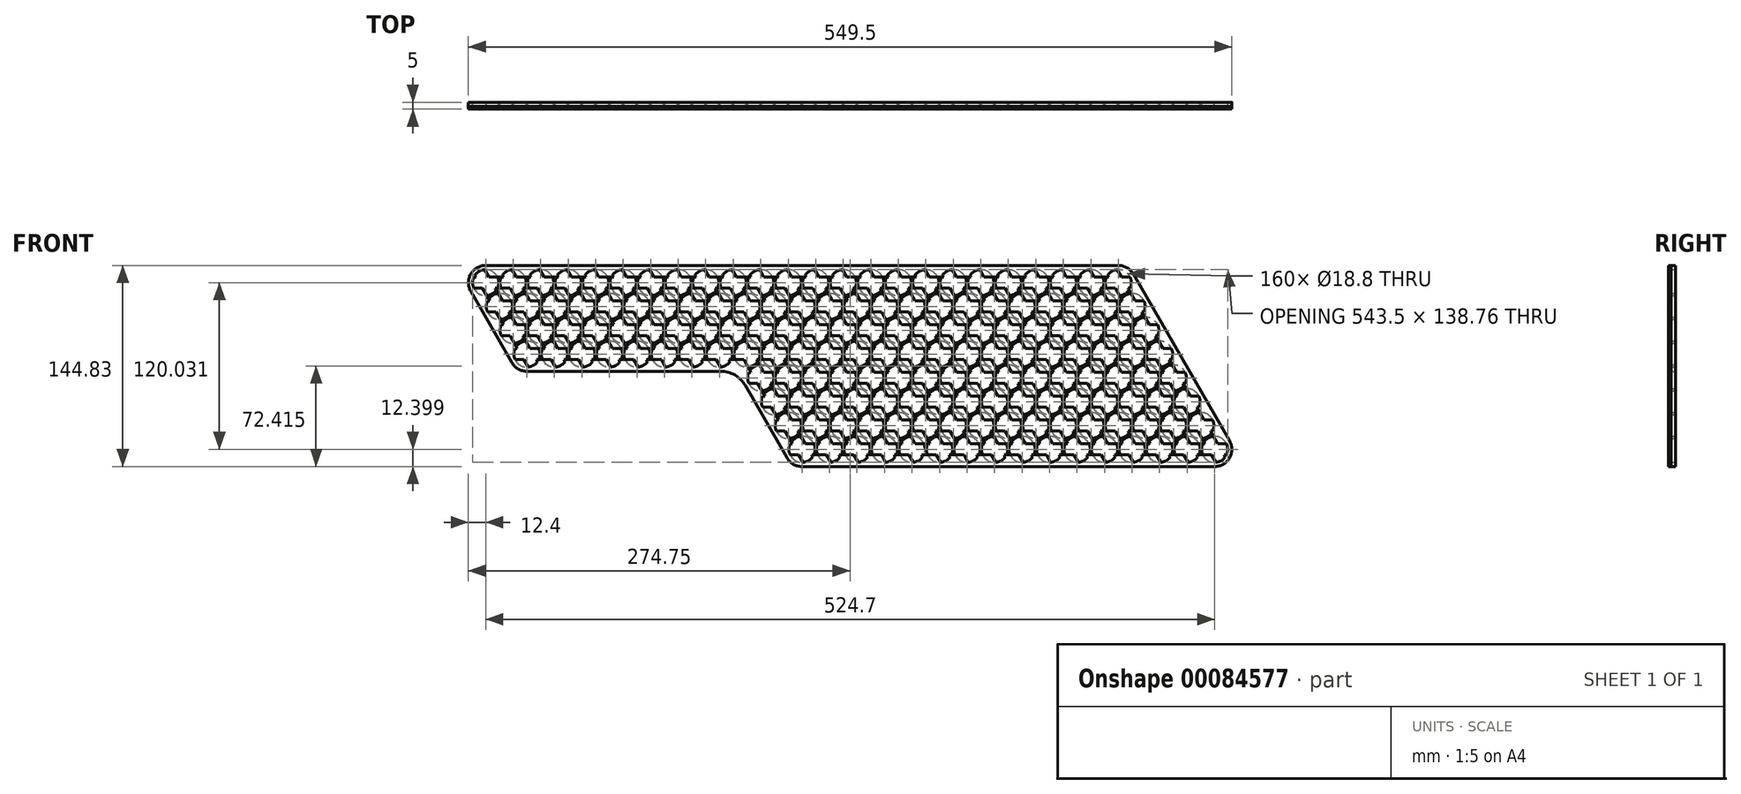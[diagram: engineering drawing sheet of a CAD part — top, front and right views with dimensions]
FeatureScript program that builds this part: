
annotation { "Feature Type Name" : "Feature", "Feature Type Description" : "" }
export const myFeature = defineFeature(function(context is Context, id is Id, definition is map)
    precondition{}
    {
        {
            var Q0;
            Q0=qCreatedBy(makeId("Front.planeOp"),FACE);
            var sketch = newSketch(context, id + "F0", { "sketchPlane" : qUnion([Q0]) });
            skCircle(sketch, "E0", {"center": v(0, 0) * mm, "radius": 9.4 * mm});
            skCircle(sketch, "E1.0.1.0", {"center": v(9.9, -17.15) * mm, "radius": 9.4 * mm});
            skCircle(sketch, "E1.0.2.0", {"center": v(19.8, -34.3) * mm, "radius": 9.4 * mm});
            skCircle(sketch, "E1.0.3.0", {"center": v(29.7, -51.44) * mm, "radius": 9.4 * mm});
            skCircle(sketch, "E1.1.0.0", {"center": v(19.8, 0) * mm, "radius": 9.4 * mm});
            skCircle(sketch, "E1.1.1.0", {"center": v(29.7, -17.15) * mm, "radius": 9.4 * mm});
            skCircle(sketch, "E1.1.2.0", {"center": v(39.6, -34.3) * mm, "radius": 9.4 * mm});
            skCircle(sketch, "E1.1.3.0", {"center": v(49.5, -51.44) * mm, "radius": 9.4 * mm});
            skCircle(sketch, "E1.2.0.0", {"center": v(39.6, 0) * mm, "radius": 9.4 * mm});
            skCircle(sketch, "E1.2.1.0", {"center": v(49.5, -17.15) * mm, "radius": 9.4 * mm});
            skCircle(sketch, "E1.2.2.0", {"center": v(59.4, -34.3) * mm, "radius": 9.4 * mm});
            skCircle(sketch, "E1.2.3.0", {"center": v(69.3, -51.44) * mm, "radius": 9.4 * mm});
            skCircle(sketch, "E1.3.0.0", {"center": v(59.4, 0) * mm, "radius": 9.4 * mm});
            skCircle(sketch, "E1.3.1.0", {"center": v(69.3, -17.15) * mm, "radius": 9.4 * mm});
            skCircle(sketch, "E1.3.2.0", {"center": v(79.2, -34.3) * mm, "radius": 9.4 * mm});
            skCircle(sketch, "E1.3.3.0", {"center": v(89.1, -51.44) * mm, "radius": 9.4 * mm});
            skCircle(sketch, "E1.4.0.0", {"center": v(79.2, 0) * mm, "radius": 9.4 * mm});
            skCircle(sketch, "E1.4.1.0", {"center": v(89.1, -17.15) * mm, "radius": 9.4 * mm});
            skCircle(sketch, "E1.4.2.0", {"center": v(99, -34.3) * mm, "radius": 9.4 * mm});
            skCircle(sketch, "E1.4.3.0", {"center": v(108.9, -51.44) * mm, "radius": 9.4 * mm});
            skCircle(sketch, "E1.5.0.0", {"center": v(99, 0) * mm, "radius": 9.4 * mm});
            skCircle(sketch, "E1.5.1.0", {"center": v(108.9, -17.15) * mm, "radius": 9.4 * mm});
            skCircle(sketch, "E1.5.2.0", {"center": v(118.8, -34.3) * mm, "radius": 9.4 * mm});
            skCircle(sketch, "E1.5.3.0", {"center": v(128.7, -51.44) * mm, "radius": 9.4 * mm});
            skCircle(sketch, "E1.6.0.0", {"center": v(118.8, 0) * mm, "radius": 9.4 * mm});
            skCircle(sketch, "E1.6.1.0", {"center": v(128.7, -17.15) * mm, "radius": 9.4 * mm});
            skCircle(sketch, "E1.6.2.0", {"center": v(138.6, -34.3) * mm, "radius": 9.4 * mm});
            skCircle(sketch, "E1.6.3.0", {"center": v(148.5, -51.44) * mm, "radius": 9.4 * mm});
            skCircle(sketch, "E1.7.0.0", {"center": v(138.6, 0) * mm, "radius": 9.4 * mm});
            skCircle(sketch, "E1.7.1.0", {"center": v(148.5, -17.15) * mm, "radius": 9.4 * mm});
            skCircle(sketch, "E1.7.2.0", {"center": v(158.4, -34.3) * mm, "radius": 9.4 * mm});
            skCircle(sketch, "E1.7.3.0", {"center": v(168.3, -51.44) * mm, "radius": 9.4 * mm});
            skCircle(sketch, "E1.8.0.0", {"center": v(158.4, 0) * mm, "radius": 9.4 * mm});
            skCircle(sketch, "E1.8.1.0", {"center": v(168.3, -17.15) * mm, "radius": 9.4 * mm});
            skCircle(sketch, "E1.8.2.0", {"center": v(178.2, -34.3) * mm, "radius": 9.4 * mm});
            skCircle(sketch, "E1.8.3.0", {"center": v(188.1, -51.44) * mm, "radius": 9.4 * mm});
            skCircle(sketch, "E1.9.0.0", {"center": v(178.2, 0) * mm, "radius": 9.4 * mm});
            skCircle(sketch, "E1.9.1.0", {"center": v(188.1, -17.15) * mm, "radius": 9.4 * mm});
            skCircle(sketch, "E1.9.2.0", {"center": v(198, -34.3) * mm, "radius": 9.4 * mm});
            skCircle(sketch, "E1.9.3.0", {"center": v(207.9, -51.44) * mm, "radius": 9.4 * mm});
            skLineSegment(sketch, "E1.direction1", {"start": v(0, 0) * mm, "end": v(19.8, 0) * mm, "construction": true});
            skLineSegment(sketch, "E1.direction2", {"start": v(0, 0) * mm, "end": v(9.9, -17.15) * mm, "construction": true});
            skCircle(sketch, "E2.0.10.0", {"center": v(198, 0) * mm, "radius": 9.4 * mm});
            skCircle(sketch, "E2.0.10.1", {"center": v(207.9, -17.15) * mm, "radius": 9.4 * mm});
            skCircle(sketch, "E2.0.10.2", {"center": v(217.8, -34.3) * mm, "radius": 9.4 * mm});
            skCircle(sketch, "E2.0.10.3", {"center": v(227.7, -51.44) * mm, "radius": 9.4 * mm});
            skCircle(sketch, "E2.0.11.0", {"center": v(217.8, 0) * mm, "radius": 9.4 * mm});
            skCircle(sketch, "E2.0.11.1", {"center": v(227.7, -17.15) * mm, "radius": 9.4 * mm});
            skCircle(sketch, "E2.0.11.2", {"center": v(237.6, -34.3) * mm, "radius": 9.4 * mm});
            skCircle(sketch, "E2.0.11.3", {"center": v(247.5, -51.44) * mm, "radius": 9.4 * mm});
            skCircle(sketch, "E2.0.12.0", {"center": v(237.6, 0) * mm, "radius": 9.4 * mm});
            skCircle(sketch, "E2.0.12.1", {"center": v(247.5, -17.15) * mm, "radius": 9.4 * mm});
            skCircle(sketch, "E2.0.12.2", {"center": v(257.4, -34.3) * mm, "radius": 9.4 * mm});
            skCircle(sketch, "E2.0.12.3", {"center": v(267.3, -51.44) * mm, "radius": 9.4 * mm});
            skCircle(sketch, "E2.0.13.0", {"center": v(257.4, 0) * mm, "radius": 9.4 * mm});
            skCircle(sketch, "E2.0.13.1", {"center": v(267.3, -17.15) * mm, "radius": 9.4 * mm});
            skCircle(sketch, "E2.0.13.2", {"center": v(277.2, -34.3) * mm, "radius": 9.4 * mm});
            skCircle(sketch, "E2.0.13.3", {"center": v(287.1, -51.44) * mm, "radius": 9.4 * mm});
            skCircle(sketch, "E2.0.14.0", {"center": v(277.2, 0) * mm, "radius": 9.4 * mm});
            skCircle(sketch, "E2.0.14.1", {"center": v(287.1, -17.15) * mm, "radius": 9.4 * mm});
            skCircle(sketch, "E2.0.14.2", {"center": v(297, -34.3) * mm, "radius": 9.4 * mm});
            skCircle(sketch, "E2.0.14.3", {"center": v(306.9, -51.44) * mm, "radius": 9.4 * mm});
            skCircle(sketch, "E2.0.15.0", {"center": v(297, 0) * mm, "radius": 9.4 * mm});
            skCircle(sketch, "E2.0.15.1", {"center": v(306.9, -17.15) * mm, "radius": 9.4 * mm});
            skCircle(sketch, "E2.0.15.2", {"center": v(316.8, -34.3) * mm, "radius": 9.4 * mm});
            skCircle(sketch, "E2.0.15.3", {"center": v(326.7, -51.44) * mm, "radius": 9.4 * mm});
            skCircle(sketch, "E2.0.16.0", {"center": v(316.8, 0) * mm, "radius": 9.4 * mm});
            skCircle(sketch, "E2.0.16.1", {"center": v(326.7, -17.15) * mm, "radius": 9.4 * mm});
            skCircle(sketch, "E2.0.16.2", {"center": v(336.6, -34.3) * mm, "radius": 9.4 * mm});
            skCircle(sketch, "E2.0.16.3", {"center": v(346.5, -51.44) * mm, "radius": 9.4 * mm});
            skCircle(sketch, "E2.0.17.0", {"center": v(336.6, 0) * mm, "radius": 9.4 * mm});
            skCircle(sketch, "E2.0.17.1", {"center": v(346.5, -17.15) * mm, "radius": 9.4 * mm});
            skCircle(sketch, "E2.0.17.2", {"center": v(356.4, -34.3) * mm, "radius": 9.4 * mm});
            skCircle(sketch, "E2.0.17.3", {"center": v(366.3, -51.44) * mm, "radius": 9.4 * mm});
            skCircle(sketch, "E2.0.18.0", {"center": v(356.4, 0) * mm, "radius": 9.4 * mm});
            skCircle(sketch, "E2.0.18.1", {"center": v(366.3, -17.15) * mm, "radius": 9.4 * mm});
            skCircle(sketch, "E2.0.18.2", {"center": v(376.2, -34.3) * mm, "radius": 9.4 * mm});
            skCircle(sketch, "E2.0.18.3", {"center": v(386.1, -51.44) * mm, "radius": 9.4 * mm});
            skCircle(sketch, "E2.0.19.0", {"center": v(376.2, 0) * mm, "radius": 9.4 * mm});
            skCircle(sketch, "E2.0.19.1", {"center": v(386.1, -17.15) * mm, "radius": 9.4 * mm});
            skCircle(sketch, "E2.0.19.2", {"center": v(396, -34.3) * mm, "radius": 9.4 * mm});
            skCircle(sketch, "E2.0.19.3", {"center": v(405.9, -51.44) * mm, "radius": 9.4 * mm});
            skCircle(sketch, "E3.0.20.0", {"center": v(396, 0) * mm, "radius": 9.4 * mm});
            skCircle(sketch, "E3.0.20.1", {"center": v(405.9, -17.15) * mm, "radius": 9.4 * mm});
            skCircle(sketch, "E3.0.20.2", {"center": v(415.8, -34.3) * mm, "radius": 9.4 * mm});
            skCircle(sketch, "E3.0.20.3", {"center": v(425.7, -51.44) * mm, "radius": 9.4 * mm});
            skCircle(sketch, "E3.0.21.0", {"center": v(415.8, 0) * mm, "radius": 9.4 * mm});
            skCircle(sketch, "E3.0.21.1", {"center": v(425.7, -17.15) * mm, "radius": 9.4 * mm});
            skCircle(sketch, "E3.0.21.2", {"center": v(435.6, -34.3) * mm, "radius": 9.4 * mm});
            skCircle(sketch, "E3.0.21.3", {"center": v(445.5, -51.44) * mm, "radius": 9.4 * mm});
            skCircle(sketch, "E3.0.22.0", {"center": v(435.6, 0) * mm, "radius": 9.4 * mm});
            skCircle(sketch, "E3.0.22.1", {"center": v(445.5, -17.15) * mm, "radius": 9.4 * mm});
            skCircle(sketch, "E3.0.22.2", {"center": v(455.4, -34.3) * mm, "radius": 9.4 * mm});
            skCircle(sketch, "E3.0.22.3", {"center": v(465.3, -51.44) * mm, "radius": 9.4 * mm});
            skCircle(sketch, "E3.0.23.0", {"center": v(455.4, 0) * mm, "radius": 9.4 * mm});
            skCircle(sketch, "E3.0.23.1", {"center": v(465.3, -17.15) * mm, "radius": 9.4 * mm});
            skCircle(sketch, "E3.0.23.2", {"center": v(475.2, -34.3) * mm, "radius": 9.4 * mm});
            skCircle(sketch, "E3.0.23.3", {"center": v(485.1, -51.44) * mm, "radius": 9.4 * mm});
            skLineSegment(sketch, "E4", {"start": v(188.1, -51.44) * mm, "end": v(158.4, 0) * mm, "construction": true});
            skLineSegment(sketch, "E5", {"start": v(237.6, 0) * mm, "end": v(207.9, -51.44) * mm, "construction": true});
            skLineSegment(sketch, "E6", {"start": v(207.9, -51.44) * mm, "end": v(188.1, -85.74) * mm, "construction": true});
            skLineSegment(sketch, "E7", {"start": v(188.1, -51.44) * mm, "end": v(207.9, -85.74) * mm, "construction": true});
            skCircle(sketch, "E8", {"center": v(198, -68.59) * mm, "radius": 9.4 * mm});
            skCircle(sketch, "E9.0.1.0", {"center": v(207.9, -85.74) * mm, "radius": 9.4 * mm});
            skCircle(sketch, "E9.0.2.0", {"center": v(217.8, -102.88) * mm, "radius": 9.4 * mm});
            skCircle(sketch, "E9.0.3.0", {"center": v(227.7, -120.03) * mm, "radius": 9.4 * mm});
            skCircle(sketch, "E9.1.0.0", {"center": v(217.8, -68.59) * mm, "radius": 9.4 * mm});
            skCircle(sketch, "E9.1.1.0", {"center": v(227.7, -85.74) * mm, "radius": 9.4 * mm});
            skCircle(sketch, "E9.1.2.0", {"center": v(237.6, -102.88) * mm, "radius": 9.4 * mm});
            skCircle(sketch, "E9.1.3.0", {"center": v(247.5, -120.03) * mm, "radius": 9.4 * mm});
            skCircle(sketch, "E9.2.0.0", {"center": v(237.6, -68.59) * mm, "radius": 9.4 * mm});
            skCircle(sketch, "E9.2.1.0", {"center": v(247.5, -85.74) * mm, "radius": 9.4 * mm});
            skCircle(sketch, "E9.2.2.0", {"center": v(257.4, -102.88) * mm, "radius": 9.4 * mm});
            skCircle(sketch, "E9.2.3.0", {"center": v(267.3, -120.03) * mm, "radius": 9.4 * mm});
            skCircle(sketch, "E9.3.0.0", {"center": v(257.4, -68.59) * mm, "radius": 9.4 * mm});
            skCircle(sketch, "E9.3.1.0", {"center": v(267.3, -85.74) * mm, "radius": 9.4 * mm});
            skCircle(sketch, "E9.3.2.0", {"center": v(277.2, -102.88) * mm, "radius": 9.4 * mm});
            skCircle(sketch, "E9.3.3.0", {"center": v(287.1, -120.03) * mm, "radius": 9.4 * mm});
            skCircle(sketch, "E9.4.0.0", {"center": v(277.2, -68.59) * mm, "radius": 9.4 * mm});
            skCircle(sketch, "E9.4.1.0", {"center": v(287.1, -85.74) * mm, "radius": 9.4 * mm});
            skCircle(sketch, "E9.4.2.0", {"center": v(297, -102.88) * mm, "radius": 9.4 * mm});
            skCircle(sketch, "E9.4.3.0", {"center": v(306.9, -120.03) * mm, "radius": 9.4 * mm});
            skCircle(sketch, "E9.5.0.0", {"center": v(297, -68.59) * mm, "radius": 9.4 * mm});
            skCircle(sketch, "E9.5.1.0", {"center": v(306.9, -85.74) * mm, "radius": 9.4 * mm});
            skCircle(sketch, "E9.5.2.0", {"center": v(316.8, -102.88) * mm, "radius": 9.4 * mm});
            skCircle(sketch, "E9.5.3.0", {"center": v(326.7, -120.03) * mm, "radius": 9.4 * mm});
            skCircle(sketch, "E9.6.0.0", {"center": v(316.8, -68.59) * mm, "radius": 9.4 * mm});
            skCircle(sketch, "E9.6.1.0", {"center": v(326.7, -85.74) * mm, "radius": 9.4 * mm});
            skCircle(sketch, "E9.6.2.0", {"center": v(336.6, -102.88) * mm, "radius": 9.4 * mm});
            skCircle(sketch, "E9.6.3.0", {"center": v(346.5, -120.03) * mm, "radius": 9.4 * mm});
            skCircle(sketch, "E9.7.0.0", {"center": v(336.6, -68.59) * mm, "radius": 9.4 * mm});
            skCircle(sketch, "E9.7.1.0", {"center": v(346.5, -85.74) * mm, "radius": 9.4 * mm});
            skCircle(sketch, "E9.7.2.0", {"center": v(356.4, -102.88) * mm, "radius": 9.4 * mm});
            skCircle(sketch, "E9.7.3.0", {"center": v(366.3, -120.03) * mm, "radius": 9.4 * mm});
            skCircle(sketch, "E9.8.0.0", {"center": v(356.4, -68.59) * mm, "radius": 9.4 * mm});
            skCircle(sketch, "E9.8.1.0", {"center": v(366.3, -85.74) * mm, "radius": 9.4 * mm});
            skCircle(sketch, "E9.8.2.0", {"center": v(376.2, -102.88) * mm, "radius": 9.4 * mm});
            skCircle(sketch, "E9.8.3.0", {"center": v(386.1, -120.03) * mm, "radius": 9.4 * mm});
            skCircle(sketch, "E9.9.0.0", {"center": v(376.2, -68.59) * mm, "radius": 9.4 * mm});
            skCircle(sketch, "E9.9.1.0", {"center": v(386.1, -85.74) * mm, "radius": 9.4 * mm});
            skCircle(sketch, "E9.9.2.0", {"center": v(396, -102.88) * mm, "radius": 9.4 * mm});
            skCircle(sketch, "E9.9.3.0", {"center": v(405.9, -120.03) * mm, "radius": 9.4 * mm});
            skCircle(sketch, "E9.10.0.0", {"center": v(396, -68.59) * mm, "radius": 9.4 * mm});
            skCircle(sketch, "E9.10.1.0", {"center": v(405.9, -85.74) * mm, "radius": 9.4 * mm});
            skCircle(sketch, "E9.10.2.0", {"center": v(415.8, -102.88) * mm, "radius": 9.4 * mm});
            skCircle(sketch, "E9.10.3.0", {"center": v(425.7, -120.03) * mm, "radius": 9.4 * mm});
            skCircle(sketch, "E9.11.0.0", {"center": v(415.8, -68.59) * mm, "radius": 9.4 * mm});
            skCircle(sketch, "E9.11.1.0", {"center": v(425.7, -85.74) * mm, "radius": 9.4 * mm});
            skCircle(sketch, "E9.11.2.0", {"center": v(435.6, -102.88) * mm, "radius": 9.4 * mm});
            skCircle(sketch, "E9.11.3.0", {"center": v(445.5, -120.03) * mm, "radius": 9.4 * mm});
            skCircle(sketch, "E9.12.0.0", {"center": v(435.6, -68.59) * mm, "radius": 9.4 * mm});
            skCircle(sketch, "E9.12.1.0", {"center": v(445.5, -85.74) * mm, "radius": 9.4 * mm});
            skCircle(sketch, "E9.12.2.0", {"center": v(455.4, -102.88) * mm, "radius": 9.4 * mm});
            skCircle(sketch, "E9.12.3.0", {"center": v(465.3, -120.03) * mm, "radius": 9.4 * mm});
            skCircle(sketch, "E9.13.0.0", {"center": v(455.4, -68.59) * mm, "radius": 9.4 * mm});
            skCircle(sketch, "E9.13.1.0", {"center": v(465.3, -85.74) * mm, "radius": 9.4 * mm});
            skCircle(sketch, "E9.13.2.0", {"center": v(475.2, -102.88) * mm, "radius": 9.4 * mm});
            skCircle(sketch, "E9.13.3.0", {"center": v(485.1, -120.03) * mm, "radius": 9.4 * mm});
            skCircle(sketch, "E9.14.0.0", {"center": v(475.2, -68.59) * mm, "radius": 9.4 * mm});
            skCircle(sketch, "E9.14.1.0", {"center": v(485.1, -85.74) * mm, "radius": 9.4 * mm});
            skCircle(sketch, "E9.14.2.0", {"center": v(495, -102.88) * mm, "radius": 9.4 * mm});
            skCircle(sketch, "E9.14.3.0", {"center": v(504.9, -120.03) * mm, "radius": 9.4 * mm});
            skCircle(sketch, "E9.15.0.0", {"center": v(495, -68.59) * mm, "radius": 9.4 * mm});
            skCircle(sketch, "E9.15.1.0", {"center": v(504.9, -85.74) * mm, "radius": 9.4 * mm});
            skCircle(sketch, "E9.15.2.0", {"center": v(514.8, -102.88) * mm, "radius": 9.4 * mm});
            skCircle(sketch, "E9.15.3.0", {"center": v(524.7, -120.03) * mm, "radius": 9.4 * mm});
            skLineSegment(sketch, "E9.direction1", {"start": v(198, -68.59) * mm, "end": v(217.8, -68.59) * mm, "construction": true});
            skLineSegment(sketch, "E9.direction2", {"start": v(198, -68.59) * mm, "end": v(207.9, -85.74) * mm, "construction": true});
            skCircle(sketch, "E10.0", {"center": v(0, 0) * mm, "radius": 12.4 * mm});
            skCircle(sketch, "E11.0", {"center": v(29.7, -51.44) * mm, "radius": 12.4 * mm});
            skCircle(sketch, "E12.0", {"center": v(455.4, 0) * mm, "radius": 12.4 * mm});
            skCircle(sketch, "E13.0", {"center": v(524.7, -120.03) * mm, "radius": 12.4 * mm});
            skCircle(sketch, "E14.0", {"center": v(227.7, -120.03) * mm, "radius": 12.4 * mm});
            skCircle(sketch, "E15.0", {"center": v(198, -68.59) * mm, "radius": 12.4 * mm});
            skLineSegment(sketch, "E16", {"start": v(-10.74, -6.2) * mm, "end": v(18.96, -57.64) * mm});
            skLineSegment(sketch, "E17", {"start": v(455.4, 12.4) * mm, "end": v(0, 12.4) * mm});
            skLineSegment(sketch, "E18", {"start": v(466.14, 6.2) * mm, "end": v(535.44, -113.83) * mm});
            skLineSegment(sketch, "E19", {"start": v(227.7, -132.43) * mm, "end": v(524.7, -132.43) * mm});
            skLineSegment(sketch, "E20", {"start": v(216.96, -126.23) * mm, "end": v(187.26, -74.79) * mm});
            skCircle(sketch, "E21.0", {"center": v(168.3, -51.44) * mm, "radius": 12.4 * mm});
            skLineSegment(sketch, "E22", {"start": v(29.7, -63.84) * mm, "end": v(168.3, -63.84) * mm});
            skLineSegment(sketch, "E23", {"start": v(168.3, -63.84) * mm, "end": v(180.94, -63.84) * mm});
            skLineSegment(sketch, "E24", {"start": v(187.26, -74.79) * mm, "end": v(180.94, -63.84) * mm});
            skSolve(sketch);
        }
        {
            var Q0;
            Q0=qSketchRegion(id+"F0",true);
            extrude(context, id + "F1", {"entities" : qUnion([Q0]), "depth" : 3 * mm});
        }
        {
            var Q0;
            Q0=makeQuery(id+"F1.opExtrude","SWEPT_EDGE",EDGE,{"disambiguationData":[OSD([sQuery(id+"F0.wireOp",EDGE,"E23"),sQuery(id+"F0.wireOp",EDGE,"E24")])]});
            fillet(context, id + "F2", {"entities" : qUnion([Q0]), "radius" : 20 * mm, "tangentPropagation" : true, "conicFillet" : false});
        }
        {
            var Q0;
            Q0=makeQuery(id+"F1.opExtrude","CAP_FACE",FACE,{"disambiguationData":[OSD([sQuery(id+"F0.wireOp",EDGE,"E0"),sQuery(id+"F0.wireOp",EDGE,"E1.0.1.0"),sQuery(id+"F0.wireOp",EDGE,"E1.0.2.0"),sQuery(id+"F0.wireOp",EDGE,"E1.0.3.0"),sQuery(id+"F0.wireOp",EDGE,"E1.1.0.0"),sQuery(id+"F0.wireOp",EDGE,"E1.1.1.0"),sQuery(id+"F0.wireOp",EDGE,"E1.1.2.0"),sQuery(id+"F0.wireOp",EDGE,"E1.1.3.0"),sQuery(id+"F0.wireOp",EDGE,"E1.2.0.0"),sQuery(id+"F0.wireOp",EDGE,"E1.2.1.0"),sQuery(id+"F0.wireOp",EDGE,"E1.2.2.0"),sQuery(id+"F0.wireOp",EDGE,"E1.2.3.0"),sQuery(id+"F0.wireOp",EDGE,"E1.3.0.0"),sQuery(id+"F0.wireOp",EDGE,"E1.3.1.0"),sQuery(id+"F0.wireOp",EDGE,"E1.3.2.0"),sQuery(id+"F0.wireOp",EDGE,"E1.3.3.0"),sQuery(id+"F0.wireOp",EDGE,"E1.4.0.0"),sQuery(id+"F0.wireOp",EDGE,"E1.4.1.0"),sQuery(id+"F0.wireOp",EDGE,"E1.4.2.0"),sQuery(id+"F0.wireOp",EDGE,"E1.4.3.0"),sQuery(id+"F0.wireOp",EDGE,"E1.5.0.0"),sQuery(id+"F0.wireOp",EDGE,"E1.5.1.0"),sQuery(id+"F0.wireOp",EDGE,"E1.5.2.0"),sQuery(id+"F0.wireOp",EDGE,"E1.5.3.0"),sQuery(id+"F0.wireOp",EDGE,"E1.6.0.0"),sQuery(id+"F0.wireOp",EDGE,"E1.6.1.0"),sQuery(id+"F0.wireOp",EDGE,"E1.6.2.0"),sQuery(id+"F0.wireOp",EDGE,"E1.6.3.0"),sQuery(id+"F0.wireOp",EDGE,"E1.7.0.0"),sQuery(id+"F0.wireOp",EDGE,"E1.7.1.0"),sQuery(id+"F0.wireOp",EDGE,"E1.7.2.0"),sQuery(id+"F0.wireOp",EDGE,"E1.7.3.0"),sQuery(id+"F0.wireOp",EDGE,"E1.8.0.0"),sQuery(id+"F0.wireOp",EDGE,"E1.8.1.0"),sQuery(id+"F0.wireOp",EDGE,"E1.8.2.0"),sQuery(id+"F0.wireOp",EDGE,"E1.8.3.0"),sQuery(id+"F0.wireOp",EDGE,"E1.9.0.0"),sQuery(id+"F0.wireOp",EDGE,"E1.9.1.0"),sQuery(id+"F0.wireOp",EDGE,"E1.9.2.0"),sQuery(id+"F0.wireOp",EDGE,"E1.9.3.0"),sQuery(id+"F0.wireOp",EDGE,"E2.0.10.0"),sQuery(id+"F0.wireOp",EDGE,"E2.0.10.1"),sQuery(id+"F0.wireOp",EDGE,"E2.0.10.2"),sQuery(id+"F0.wireOp",EDGE,"E2.0.10.3"),sQuery(id+"F0.wireOp",EDGE,"E2.0.11.0"),sQuery(id+"F0.wireOp",EDGE,"E2.0.11.1"),sQuery(id+"F0.wireOp",EDGE,"E2.0.11.2"),sQuery(id+"F0.wireOp",EDGE,"E2.0.11.3"),sQuery(id+"F0.wireOp",EDGE,"E2.0.12.0"),sQuery(id+"F0.wireOp",EDGE,"E2.0.12.1"),sQuery(id+"F0.wireOp",EDGE,"E2.0.12.2"),sQuery(id+"F0.wireOp",EDGE,"E2.0.12.3"),sQuery(id+"F0.wireOp",EDGE,"E2.0.13.0"),sQuery(id+"F0.wireOp",EDGE,"E2.0.13.1"),sQuery(id+"F0.wireOp",EDGE,"E2.0.13.2"),sQuery(id+"F0.wireOp",EDGE,"E2.0.13.3"),sQuery(id+"F0.wireOp",EDGE,"E2.0.14.0"),sQuery(id+"F0.wireOp",EDGE,"E2.0.14.1"),sQuery(id+"F0.wireOp",EDGE,"E2.0.14.2"),sQuery(id+"F0.wireOp",EDGE,"E2.0.14.3"),sQuery(id+"F0.wireOp",EDGE,"E2.0.15.0"),sQuery(id+"F0.wireOp",EDGE,"E2.0.15.1"),sQuery(id+"F0.wireOp",EDGE,"E2.0.15.2"),sQuery(id+"F0.wireOp",EDGE,"E2.0.15.3"),sQuery(id+"F0.wireOp",EDGE,"E2.0.16.0"),sQuery(id+"F0.wireOp",EDGE,"E2.0.16.1"),sQuery(id+"F0.wireOp",EDGE,"E2.0.16.2"),sQuery(id+"F0.wireOp",EDGE,"E2.0.16.3"),sQuery(id+"F0.wireOp",EDGE,"E2.0.17.0"),sQuery(id+"F0.wireOp",EDGE,"E2.0.17.1"),sQuery(id+"F0.wireOp",EDGE,"E2.0.17.2"),sQuery(id+"F0.wireOp",EDGE,"E2.0.17.3"),sQuery(id+"F0.wireOp",EDGE,"E2.0.18.0"),sQuery(id+"F0.wireOp",EDGE,"E2.0.18.1"),sQuery(id+"F0.wireOp",EDGE,"E2.0.18.2"),sQuery(id+"F0.wireOp",EDGE,"E2.0.18.3"),sQuery(id+"F0.wireOp",EDGE,"E2.0.19.0"),sQuery(id+"F0.wireOp",EDGE,"E2.0.19.1"),sQuery(id+"F0.wireOp",EDGE,"E2.0.19.2"),sQuery(id+"F0.wireOp",EDGE,"E2.0.19.3"),sQuery(id+"F0.wireOp",EDGE,"E3.0.20.0"),sQuery(id+"F0.wireOp",EDGE,"E3.0.20.1"),sQuery(id+"F0.wireOp",EDGE,"E3.0.20.2"),sQuery(id+"F0.wireOp",EDGE,"E3.0.20.3"),sQuery(id+"F0.wireOp",EDGE,"E3.0.21.0"),sQuery(id+"F0.wireOp",EDGE,"E3.0.21.1"),sQuery(id+"F0.wireOp",EDGE,"E3.0.21.2"),sQuery(id+"F0.wireOp",EDGE,"E3.0.21.3"),sQuery(id+"F0.wireOp",EDGE,"E3.0.22.0"),sQuery(id+"F0.wireOp",EDGE,"E3.0.22.1"),sQuery(id+"F0.wireOp",EDGE,"E3.0.22.2"),sQuery(id+"F0.wireOp",EDGE,"E3.0.22.3"),sQuery(id+"F0.wireOp",EDGE,"E3.0.23.0"),sQuery(id+"F0.wireOp",EDGE,"E3.0.23.1"),sQuery(id+"F0.wireOp",EDGE,"E3.0.23.2"),sQuery(id+"F0.wireOp",EDGE,"E3.0.23.3"),sQuery(id+"F0.wireOp",EDGE,"E8"),sQuery(id+"F0.wireOp",EDGE,"E9.0.1.0"),sQuery(id+"F0.wireOp",EDGE,"E9.0.2.0"),sQuery(id+"F0.wireOp",EDGE,"E9.0.3.0"),sQuery(id+"F0.wireOp",EDGE,"E9.1.0.0"),sQuery(id+"F0.wireOp",EDGE,"E9.1.1.0"),sQuery(id+"F0.wireOp",EDGE,"E9.1.2.0"),sQuery(id+"F0.wireOp",EDGE,"E9.1.3.0"),sQuery(id+"F0.wireOp",EDGE,"E9.2.0.0"),sQuery(id+"F0.wireOp",EDGE,"E9.2.1.0"),sQuery(id+"F0.wireOp",EDGE,"E9.2.2.0"),sQuery(id+"F0.wireOp",EDGE,"E9.2.3.0"),sQuery(id+"F0.wireOp",EDGE,"E9.3.0.0"),sQuery(id+"F0.wireOp",EDGE,"E9.3.1.0"),sQuery(id+"F0.wireOp",EDGE,"E9.3.2.0"),sQuery(id+"F0.wireOp",EDGE,"E9.3.3.0"),sQuery(id+"F0.wireOp",EDGE,"E9.4.0.0"),sQuery(id+"F0.wireOp",EDGE,"E9.4.1.0"),sQuery(id+"F0.wireOp",EDGE,"E9.4.2.0"),sQuery(id+"F0.wireOp",EDGE,"E9.4.3.0"),sQuery(id+"F0.wireOp",EDGE,"E9.5.0.0"),sQuery(id+"F0.wireOp",EDGE,"E9.5.1.0"),sQuery(id+"F0.wireOp",EDGE,"E9.5.2.0"),sQuery(id+"F0.wireOp",EDGE,"E9.5.3.0"),sQuery(id+"F0.wireOp",EDGE,"E9.6.0.0"),sQuery(id+"F0.wireOp",EDGE,"E9.6.1.0"),sQuery(id+"F0.wireOp",EDGE,"E9.6.2.0"),sQuery(id+"F0.wireOp",EDGE,"E9.6.3.0"),sQuery(id+"F0.wireOp",EDGE,"E9.7.0.0"),sQuery(id+"F0.wireOp",EDGE,"E9.7.1.0"),sQuery(id+"F0.wireOp",EDGE,"E9.7.2.0"),sQuery(id+"F0.wireOp",EDGE,"E9.7.3.0"),sQuery(id+"F0.wireOp",EDGE,"E9.8.0.0"),sQuery(id+"F0.wireOp",EDGE,"E9.8.1.0"),sQuery(id+"F0.wireOp",EDGE,"E9.8.2.0"),sQuery(id+"F0.wireOp",EDGE,"E9.8.3.0"),sQuery(id+"F0.wireOp",EDGE,"E9.9.0.0"),sQuery(id+"F0.wireOp",EDGE,"E9.9.1.0"),sQuery(id+"F0.wireOp",EDGE,"E9.9.2.0"),sQuery(id+"F0.wireOp",EDGE,"E9.9.3.0"),sQuery(id+"F0.wireOp",EDGE,"E9.10.0.0"),sQuery(id+"F0.wireOp",EDGE,"E9.10.1.0"),sQuery(id+"F0.wireOp",EDGE,"E9.10.2.0"),sQuery(id+"F0.wireOp",EDGE,"E9.10.3.0"),sQuery(id+"F0.wireOp",EDGE,"E9.11.0.0"),sQuery(id+"F0.wireOp",EDGE,"E9.11.1.0"),sQuery(id+"F0.wireOp",EDGE,"E9.11.2.0"),sQuery(id+"F0.wireOp",EDGE,"E9.11.3.0"),sQuery(id+"F0.wireOp",EDGE,"E9.12.0.0"),sQuery(id+"F0.wireOp",EDGE,"E9.12.1.0"),sQuery(id+"F0.wireOp",EDGE,"E9.12.2.0"),sQuery(id+"F0.wireOp",EDGE,"E9.12.3.0"),sQuery(id+"F0.wireOp",EDGE,"E9.13.0.0"),sQuery(id+"F0.wireOp",EDGE,"E9.13.1.0"),sQuery(id+"F0.wireOp",EDGE,"E9.13.2.0"),sQuery(id+"F0.wireOp",EDGE,"E9.13.3.0"),sQuery(id+"F0.wireOp",EDGE,"E9.14.0.0"),sQuery(id+"F0.wireOp",EDGE,"E9.14.1.0"),sQuery(id+"F0.wireOp",EDGE,"E9.14.2.0"),sQuery(id+"F0.wireOp",EDGE,"E9.14.3.0"),sQuery(id+"F0.wireOp",EDGE,"E9.15.0.0"),sQuery(id+"F0.wireOp",EDGE,"E9.15.1.0"),sQuery(id+"F0.wireOp",EDGE,"E9.15.2.0"),sQuery(id+"F0.wireOp",EDGE,"E9.15.3.0"),sQuery(id+"F0.wireOp",EDGE,"E10.0"),sQuery(id+"F0.wireOp",EDGE,"E11.0"),sQuery(id+"F0.wireOp",EDGE,"E12.0"),sQuery(id+"F0.wireOp",EDGE,"E13.0"),sQuery(id+"F0.wireOp",EDGE,"E14.0"),sQuery(id+"F0.wireOp",EDGE,"E16"),sQuery(id+"F0.wireOp",EDGE,"E17"),sQuery(id+"F0.wireOp",EDGE,"E18"),sQuery(id+"F0.wireOp",EDGE,"E19"),sQuery(id+"F0.wireOp",EDGE,"E20"),sQuery(id+"F0.wireOp",EDGE,"E22"),sQuery(id+"F0.wireOp",EDGE,"E23"),sQuery(id+"F0.wireOp",EDGE,"E24")])],"isStart":false});
            var sketch = newSketch(context, id + "F3", { "sketchPlane" : qUnion([Q0]) });
            skLineSegment(sketch, "E25.0", {"start": v(455.4, 12.4) * mm, "end": v(0, 12.4) * mm});
            skLineSegment(sketch, "E25.1", {"start": v(-10.74, -6.2) * mm, "end": v(18.96, -57.64) * mm});
            skLineSegment(sketch, "E25.2", {"start": v(29.7, -63.84) * mm, "end": v(169.4, -63.84) * mm});
            skLineSegment(sketch, "E25.3", {"start": v(216.96, -126.23) * mm, "end": v(186.71, -73.84) * mm});
            skLineSegment(sketch, "E25.4", {"start": v(227.7, -132.43) * mm, "end": v(524.7, -132.43) * mm});
            skLineSegment(sketch, "E25.5", {"start": v(466.14, 6.2) * mm, "end": v(535.44, -113.83) * mm});
            skArc(sketch, "E25.6", {"start": v(466.14, 6.2) * mm, "mid": v(461.6, 10.74) * mm, "end": v(455.4, 12.4) * mm});
            skArc(sketch, "E25.7", {"start": v(524.7, -132.43) * mm, "mid": v(535.44, -126.23) * mm, "end": v(535.44, -113.83) * mm});
            skArc(sketch, "E25.8", {"start": v(216.96, -126.23) * mm, "mid": v(221.5, -130.77) * mm, "end": v(227.7, -132.43) * mm});
            skArc(sketch, "E25.9", {"start": v(169.4, -63.84) * mm, "mid": v(179.4, -66.52) * mm, "end": v(186.71, -73.84) * mm});
            skArc(sketch, "E25.10", {"start": v(18.96, -57.64) * mm, "mid": v(23.5, -62.18) * mm, "end": v(29.7, -63.84) * mm});
            skArc(sketch, "E25.11", {"start": v(0, 12.4) * mm, "mid": v(-10.74, 6.2) * mm, "end": v(-10.74, -6.2) * mm});
            skSolve(sketch);
        }
        {
            var Q0;
            Q0 = qSketchRegion(id + "F3", true);
            extrude(context, id + "F4", {"entities" : qUnion([Q0]), "depth" : 2 * mm});
        }
        {
            var Q0;
            Q0=makeQuery(id+"F1.opExtrude","CAP_FACE",FACE,{"disambiguationData":[OSD([sQuery(id+"F0.wireOp",EDGE,"E0"),sQuery(id+"F0.wireOp",EDGE,"E1.0.1.0"),sQuery(id+"F0.wireOp",EDGE,"E1.0.2.0"),sQuery(id+"F0.wireOp",EDGE,"E1.0.3.0"),sQuery(id+"F0.wireOp",EDGE,"E1.1.0.0"),sQuery(id+"F0.wireOp",EDGE,"E1.1.1.0"),sQuery(id+"F0.wireOp",EDGE,"E1.1.2.0"),sQuery(id+"F0.wireOp",EDGE,"E1.1.3.0"),sQuery(id+"F0.wireOp",EDGE,"E1.2.0.0"),sQuery(id+"F0.wireOp",EDGE,"E1.2.1.0"),sQuery(id+"F0.wireOp",EDGE,"E1.2.2.0"),sQuery(id+"F0.wireOp",EDGE,"E1.2.3.0"),sQuery(id+"F0.wireOp",EDGE,"E1.3.0.0"),sQuery(id+"F0.wireOp",EDGE,"E1.3.1.0"),sQuery(id+"F0.wireOp",EDGE,"E1.3.2.0"),sQuery(id+"F0.wireOp",EDGE,"E1.3.3.0"),sQuery(id+"F0.wireOp",EDGE,"E1.4.0.0"),sQuery(id+"F0.wireOp",EDGE,"E1.4.1.0"),sQuery(id+"F0.wireOp",EDGE,"E1.4.2.0"),sQuery(id+"F0.wireOp",EDGE,"E1.4.3.0"),sQuery(id+"F0.wireOp",EDGE,"E1.5.0.0"),sQuery(id+"F0.wireOp",EDGE,"E1.5.1.0"),sQuery(id+"F0.wireOp",EDGE,"E1.5.2.0"),sQuery(id+"F0.wireOp",EDGE,"E1.5.3.0"),sQuery(id+"F0.wireOp",EDGE,"E1.6.0.0"),sQuery(id+"F0.wireOp",EDGE,"E1.6.1.0"),sQuery(id+"F0.wireOp",EDGE,"E1.6.2.0"),sQuery(id+"F0.wireOp",EDGE,"E1.6.3.0"),sQuery(id+"F0.wireOp",EDGE,"E1.7.0.0"),sQuery(id+"F0.wireOp",EDGE,"E1.7.1.0"),sQuery(id+"F0.wireOp",EDGE,"E1.7.2.0"),sQuery(id+"F0.wireOp",EDGE,"E1.7.3.0"),sQuery(id+"F0.wireOp",EDGE,"E1.8.0.0"),sQuery(id+"F0.wireOp",EDGE,"E1.8.1.0"),sQuery(id+"F0.wireOp",EDGE,"E1.8.2.0"),sQuery(id+"F0.wireOp",EDGE,"E1.8.3.0"),sQuery(id+"F0.wireOp",EDGE,"E1.9.0.0"),sQuery(id+"F0.wireOp",EDGE,"E1.9.1.0"),sQuery(id+"F0.wireOp",EDGE,"E1.9.2.0"),sQuery(id+"F0.wireOp",EDGE,"E1.9.3.0"),sQuery(id+"F0.wireOp",EDGE,"E2.0.10.0"),sQuery(id+"F0.wireOp",EDGE,"E2.0.10.1"),sQuery(id+"F0.wireOp",EDGE,"E2.0.10.2"),sQuery(id+"F0.wireOp",EDGE,"E2.0.10.3"),sQuery(id+"F0.wireOp",EDGE,"E2.0.11.0"),sQuery(id+"F0.wireOp",EDGE,"E2.0.11.1"),sQuery(id+"F0.wireOp",EDGE,"E2.0.11.2"),sQuery(id+"F0.wireOp",EDGE,"E2.0.11.3"),sQuery(id+"F0.wireOp",EDGE,"E2.0.12.0"),sQuery(id+"F0.wireOp",EDGE,"E2.0.12.1"),sQuery(id+"F0.wireOp",EDGE,"E2.0.12.2"),sQuery(id+"F0.wireOp",EDGE,"E2.0.12.3"),sQuery(id+"F0.wireOp",EDGE,"E2.0.13.0"),sQuery(id+"F0.wireOp",EDGE,"E2.0.13.1"),sQuery(id+"F0.wireOp",EDGE,"E2.0.13.2"),sQuery(id+"F0.wireOp",EDGE,"E2.0.13.3"),sQuery(id+"F0.wireOp",EDGE,"E2.0.14.0"),sQuery(id+"F0.wireOp",EDGE,"E2.0.14.1"),sQuery(id+"F0.wireOp",EDGE,"E2.0.14.2"),sQuery(id+"F0.wireOp",EDGE,"E2.0.14.3"),sQuery(id+"F0.wireOp",EDGE,"E2.0.15.0"),sQuery(id+"F0.wireOp",EDGE,"E2.0.15.1"),sQuery(id+"F0.wireOp",EDGE,"E2.0.15.2"),sQuery(id+"F0.wireOp",EDGE,"E2.0.15.3"),sQuery(id+"F0.wireOp",EDGE,"E2.0.16.0"),sQuery(id+"F0.wireOp",EDGE,"E2.0.16.1"),sQuery(id+"F0.wireOp",EDGE,"E2.0.16.2"),sQuery(id+"F0.wireOp",EDGE,"E2.0.16.3"),sQuery(id+"F0.wireOp",EDGE,"E2.0.17.0"),sQuery(id+"F0.wireOp",EDGE,"E2.0.17.1"),sQuery(id+"F0.wireOp",EDGE,"E2.0.17.2"),sQuery(id+"F0.wireOp",EDGE,"E2.0.17.3"),sQuery(id+"F0.wireOp",EDGE,"E2.0.18.0"),sQuery(id+"F0.wireOp",EDGE,"E2.0.18.1"),sQuery(id+"F0.wireOp",EDGE,"E2.0.18.2"),sQuery(id+"F0.wireOp",EDGE,"E2.0.18.3"),sQuery(id+"F0.wireOp",EDGE,"E2.0.19.0"),sQuery(id+"F0.wireOp",EDGE,"E2.0.19.1"),sQuery(id+"F0.wireOp",EDGE,"E2.0.19.2"),sQuery(id+"F0.wireOp",EDGE,"E2.0.19.3"),sQuery(id+"F0.wireOp",EDGE,"E3.0.20.0"),sQuery(id+"F0.wireOp",EDGE,"E3.0.20.1"),sQuery(id+"F0.wireOp",EDGE,"E3.0.20.2"),sQuery(id+"F0.wireOp",EDGE,"E3.0.20.3"),sQuery(id+"F0.wireOp",EDGE,"E3.0.21.0"),sQuery(id+"F0.wireOp",EDGE,"E3.0.21.1"),sQuery(id+"F0.wireOp",EDGE,"E3.0.21.2"),sQuery(id+"F0.wireOp",EDGE,"E3.0.21.3"),sQuery(id+"F0.wireOp",EDGE,"E3.0.22.0"),sQuery(id+"F0.wireOp",EDGE,"E3.0.22.1"),sQuery(id+"F0.wireOp",EDGE,"E3.0.22.2"),sQuery(id+"F0.wireOp",EDGE,"E3.0.22.3"),sQuery(id+"F0.wireOp",EDGE,"E3.0.23.0"),sQuery(id+"F0.wireOp",EDGE,"E3.0.23.1"),sQuery(id+"F0.wireOp",EDGE,"E3.0.23.2"),sQuery(id+"F0.wireOp",EDGE,"E3.0.23.3"),sQuery(id+"F0.wireOp",EDGE,"E8"),sQuery(id+"F0.wireOp",EDGE,"E9.0.1.0"),sQuery(id+"F0.wireOp",EDGE,"E9.0.2.0"),sQuery(id+"F0.wireOp",EDGE,"E9.0.3.0"),sQuery(id+"F0.wireOp",EDGE,"E9.1.0.0"),sQuery(id+"F0.wireOp",EDGE,"E9.1.1.0"),sQuery(id+"F0.wireOp",EDGE,"E9.1.2.0"),sQuery(id+"F0.wireOp",EDGE,"E9.1.3.0"),sQuery(id+"F0.wireOp",EDGE,"E9.2.0.0"),sQuery(id+"F0.wireOp",EDGE,"E9.2.1.0"),sQuery(id+"F0.wireOp",EDGE,"E9.2.2.0"),sQuery(id+"F0.wireOp",EDGE,"E9.2.3.0"),sQuery(id+"F0.wireOp",EDGE,"E9.3.0.0"),sQuery(id+"F0.wireOp",EDGE,"E9.3.1.0"),sQuery(id+"F0.wireOp",EDGE,"E9.3.2.0"),sQuery(id+"F0.wireOp",EDGE,"E9.3.3.0"),sQuery(id+"F0.wireOp",EDGE,"E9.4.0.0"),sQuery(id+"F0.wireOp",EDGE,"E9.4.1.0"),sQuery(id+"F0.wireOp",EDGE,"E9.4.2.0"),sQuery(id+"F0.wireOp",EDGE,"E9.4.3.0"),sQuery(id+"F0.wireOp",EDGE,"E9.5.0.0"),sQuery(id+"F0.wireOp",EDGE,"E9.5.1.0"),sQuery(id+"F0.wireOp",EDGE,"E9.5.2.0"),sQuery(id+"F0.wireOp",EDGE,"E9.5.3.0"),sQuery(id+"F0.wireOp",EDGE,"E9.6.0.0"),sQuery(id+"F0.wireOp",EDGE,"E9.6.1.0"),sQuery(id+"F0.wireOp",EDGE,"E9.6.2.0"),sQuery(id+"F0.wireOp",EDGE,"E9.6.3.0"),sQuery(id+"F0.wireOp",EDGE,"E9.7.0.0"),sQuery(id+"F0.wireOp",EDGE,"E9.7.1.0"),sQuery(id+"F0.wireOp",EDGE,"E9.7.2.0"),sQuery(id+"F0.wireOp",EDGE,"E9.7.3.0"),sQuery(id+"F0.wireOp",EDGE,"E9.8.0.0"),sQuery(id+"F0.wireOp",EDGE,"E9.8.1.0"),sQuery(id+"F0.wireOp",EDGE,"E9.8.2.0"),sQuery(id+"F0.wireOp",EDGE,"E9.8.3.0"),sQuery(id+"F0.wireOp",EDGE,"E9.9.0.0"),sQuery(id+"F0.wireOp",EDGE,"E9.9.1.0"),sQuery(id+"F0.wireOp",EDGE,"E9.9.2.0"),sQuery(id+"F0.wireOp",EDGE,"E9.9.3.0"),sQuery(id+"F0.wireOp",EDGE,"E9.10.0.0"),sQuery(id+"F0.wireOp",EDGE,"E9.10.1.0"),sQuery(id+"F0.wireOp",EDGE,"E9.10.2.0"),sQuery(id+"F0.wireOp",EDGE,"E9.10.3.0"),sQuery(id+"F0.wireOp",EDGE,"E9.11.0.0"),sQuery(id+"F0.wireOp",EDGE,"E9.11.1.0"),sQuery(id+"F0.wireOp",EDGE,"E9.11.2.0"),sQuery(id+"F0.wireOp",EDGE,"E9.11.3.0"),sQuery(id+"F0.wireOp",EDGE,"E9.12.0.0"),sQuery(id+"F0.wireOp",EDGE,"E9.12.1.0"),sQuery(id+"F0.wireOp",EDGE,"E9.12.2.0"),sQuery(id+"F0.wireOp",EDGE,"E9.12.3.0"),sQuery(id+"F0.wireOp",EDGE,"E9.13.0.0"),sQuery(id+"F0.wireOp",EDGE,"E9.13.1.0"),sQuery(id+"F0.wireOp",EDGE,"E9.13.2.0"),sQuery(id+"F0.wireOp",EDGE,"E9.13.3.0"),sQuery(id+"F0.wireOp",EDGE,"E9.14.0.0"),sQuery(id+"F0.wireOp",EDGE,"E9.14.1.0"),sQuery(id+"F0.wireOp",EDGE,"E9.14.2.0"),sQuery(id+"F0.wireOp",EDGE,"E9.14.3.0"),sQuery(id+"F0.wireOp",EDGE,"E9.15.0.0"),sQuery(id+"F0.wireOp",EDGE,"E9.15.1.0"),sQuery(id+"F0.wireOp",EDGE,"E9.15.2.0"),sQuery(id+"F0.wireOp",EDGE,"E9.15.3.0"),sQuery(id+"F0.wireOp",EDGE,"E10.0"),sQuery(id+"F0.wireOp",EDGE,"E11.0"),sQuery(id+"F0.wireOp",EDGE,"E12.0"),sQuery(id+"F0.wireOp",EDGE,"E13.0"),sQuery(id+"F0.wireOp",EDGE,"E14.0"),sQuery(id+"F0.wireOp",EDGE,"E16"),sQuery(id+"F0.wireOp",EDGE,"E17"),sQuery(id+"F0.wireOp",EDGE,"E18"),sQuery(id+"F0.wireOp",EDGE,"E19"),sQuery(id+"F0.wireOp",EDGE,"E20"),sQuery(id+"F0.wireOp",EDGE,"E22"),sQuery(id+"F0.wireOp",EDGE,"E23"),sQuery(id+"F0.wireOp",EDGE,"E24")])],"isStart":false});
            var sketch = newSketch(context, id + "F5", { "sketchPlane" : qUnion([Q0]) });
            skArc(sketch, "E26.0", {"start": v(-8.5, 4) * mm, "mid": v(-9.4, 0) * mm, "end": v(-8.5, -4) * mm});
            skArc(sketch, "E26.1", {"start": v(21.2, -47.44) * mm, "mid": v(20.3, -51.44) * mm, "end": v(21.2, -55.44) * mm});
            skLineSegment(sketch, "E27", {"start": v(0, 0) * mm, "end": v(455.4, 0) * mm, "construction": true});
            skLineSegment(sketch, "E28", {"start": v(0, 0) * mm, "end": v(29.7, -51.44) * mm, "construction": true});
            skLineSegment(sketch, "E29", {"start": v(198, -68.59) * mm, "end": v(495, -68.59) * mm, "construction": true});
            skLineSegment(sketch, "E30", {"start": v(198, -68.59) * mm, "end": v(227.7, -120.03) * mm, "construction": true});
            skLineSegment(sketch, "E31.0.left", {"start": v(0, 4) * mm, "end": v(463.9, 4) * mm});
            skLineSegment(sketch, "E31.0.right", {"start": v(0, -4) * mm, "end": v(463.9, -4) * mm});
            skLineSegment(sketch, "E32", {"start": v(0, 4) * mm, "end": v(-8.5, 4) * mm});
            skLineSegment(sketch, "E33", {"start": v(0, -4) * mm, "end": v(-8.5, -4) * mm});
            skArc(sketch, "E34.trimOffspring", {"start": v(463.9, -4) * mm, "mid": v(464.8, 0) * mm, "end": v(463.9, 4) * mm});
            skArc(sketch, "E35.0.1.0", {"start": v(1.4, -13.15) * mm, "mid": v(0.5, -17.15) * mm, "end": v(1.4, -21.15) * mm});
            skLineSegment(sketch, "E35.0.1.1", {"start": v(9.9, -13.15) * mm, "end": v(1.4, -13.15) * mm});
            skLineSegment(sketch, "E35.0.1.2", {"start": v(9.9, -21.15) * mm, "end": v(1.4, -21.15) * mm});
            skLineSegment(sketch, "E35.0.1.3", {"start": v(9.9, -13.15) * mm, "end": v(473.8, -13.15) * mm});
            skLineSegment(sketch, "E35.0.1.4", {"start": v(9.9, -21.15) * mm, "end": v(473.8, -21.15) * mm});
            skArc(sketch, "E35.0.1.5", {"start": v(473.8, -21.15) * mm, "mid": v(474.7, -17.15) * mm, "end": v(473.8, -13.15) * mm});
            skArc(sketch, "E35.0.2.0", {"start": v(11.3, -30.3) * mm, "mid": v(10.4, -34.3) * mm, "end": v(11.3, -38.3) * mm});
            skLineSegment(sketch, "E35.0.2.1", {"start": v(19.8, -30.3) * mm, "end": v(11.3, -30.3) * mm});
            skLineSegment(sketch, "E35.0.2.2", {"start": v(19.8, -38.3) * mm, "end": v(11.3, -38.3) * mm});
            skLineSegment(sketch, "E35.0.2.3", {"start": v(19.8, -30.3) * mm, "end": v(483.7, -30.3) * mm});
            skLineSegment(sketch, "E35.0.2.4", {"start": v(19.8, -38.3) * mm, "end": v(483.7, -38.3) * mm});
            skArc(sketch, "E35.0.2.5", {"start": v(483.7, -38.3) * mm, "mid": v(484.6, -34.3) * mm, "end": v(483.7, -30.3) * mm});
            skLineSegment(sketch, "E35.0.3.1", {"start": v(29.7, -47.44) * mm, "end": v(21.2, -47.44) * mm});
            skLineSegment(sketch, "E35.0.3.2", {"start": v(29.7, -55.44) * mm, "end": v(21.2, -55.44) * mm});
            skLineSegment(sketch, "E35.0.3.3", {"start": v(29.7, -47.44) * mm, "end": v(493.6, -47.44) * mm});
            skLineSegment(sketch, "E35.0.3.4", {"start": v(29.7, -55.44) * mm, "end": v(493.6, -55.44) * mm});
            skArc(sketch, "E35.0.3.5", {"start": v(493.6, -55.44) * mm, "mid": v(494.5, -51.44) * mm, "end": v(493.6, -47.44) * mm});
            skLineSegment(sketch, "E35.direction1", {"start": v(-8.5, -4) * mm, "end": v(16.5, -4) * mm, "construction": true});
            skLineSegment(sketch, "E35.direction2", {"start": v(-8.5, -4) * mm, "end": v(1.4, -21.15) * mm, "construction": true});
            skSolve(sketch);
        }
        {
            var Q0;
            Q0 = qSketchRegion(id + "F5", true);
            var Q1;
            Q1=makeQuery(id+"F4.opExtrude","CAP_FACE",FACE,{"disambiguationData":[OSD([sQuery(id+"F3.wireOp",EDGE,"E25.0"),sQuery(id+"F3.wireOp",EDGE,"E25.1"),sQuery(id+"F3.wireOp",EDGE,"E25.2"),sQuery(id+"F3.wireOp",EDGE,"E25.3"),sQuery(id+"F3.wireOp",EDGE,"E25.4"),sQuery(id+"F3.wireOp",EDGE,"E25.5"),sQuery(id+"F3.wireOp",EDGE,"E25.6"),sQuery(id+"F3.wireOp",EDGE,"E25.7"),sQuery(id+"F3.wireOp",EDGE,"E25.8"),sQuery(id+"F3.wireOp",EDGE,"E25.9"),sQuery(id+"F3.wireOp",EDGE,"E25.10"),sQuery(id+"F3.wireOp",EDGE,"E25.11")])],"isStart":false});
            extrude(context, id + "F6", {"entities" : qUnion([Q0]), "operationType" : NewBodyOperationType.REMOVE, "endBound" : BoundingType.UP_TO_SURFACE, "endBoundEntityFace" : qUnion([Q1]), "depth" : 25 * mm});
        }
        {
            var Q0;
            Q0=makeQuery(id+"F1.opExtrude","CAP_FACE",FACE,{"disambiguationData":[OSD([sQuery(id+"F0.wireOp",EDGE,"E0"),sQuery(id+"F0.wireOp",EDGE,"E1.0.1.0"),sQuery(id+"F0.wireOp",EDGE,"E1.0.2.0"),sQuery(id+"F0.wireOp",EDGE,"E1.0.3.0"),sQuery(id+"F0.wireOp",EDGE,"E1.1.0.0"),sQuery(id+"F0.wireOp",EDGE,"E1.1.1.0"),sQuery(id+"F0.wireOp",EDGE,"E1.1.2.0"),sQuery(id+"F0.wireOp",EDGE,"E1.1.3.0"),sQuery(id+"F0.wireOp",EDGE,"E1.2.0.0"),sQuery(id+"F0.wireOp",EDGE,"E1.2.1.0"),sQuery(id+"F0.wireOp",EDGE,"E1.2.2.0"),sQuery(id+"F0.wireOp",EDGE,"E1.2.3.0"),sQuery(id+"F0.wireOp",EDGE,"E1.3.0.0"),sQuery(id+"F0.wireOp",EDGE,"E1.3.1.0"),sQuery(id+"F0.wireOp",EDGE,"E1.3.2.0"),sQuery(id+"F0.wireOp",EDGE,"E1.3.3.0"),sQuery(id+"F0.wireOp",EDGE,"E1.4.0.0"),sQuery(id+"F0.wireOp",EDGE,"E1.4.1.0"),sQuery(id+"F0.wireOp",EDGE,"E1.4.2.0"),sQuery(id+"F0.wireOp",EDGE,"E1.4.3.0"),sQuery(id+"F0.wireOp",EDGE,"E1.5.0.0"),sQuery(id+"F0.wireOp",EDGE,"E1.5.1.0"),sQuery(id+"F0.wireOp",EDGE,"E1.5.2.0"),sQuery(id+"F0.wireOp",EDGE,"E1.5.3.0"),sQuery(id+"F0.wireOp",EDGE,"E1.6.0.0"),sQuery(id+"F0.wireOp",EDGE,"E1.6.1.0"),sQuery(id+"F0.wireOp",EDGE,"E1.6.2.0"),sQuery(id+"F0.wireOp",EDGE,"E1.6.3.0"),sQuery(id+"F0.wireOp",EDGE,"E1.7.0.0"),sQuery(id+"F0.wireOp",EDGE,"E1.7.1.0"),sQuery(id+"F0.wireOp",EDGE,"E1.7.2.0"),sQuery(id+"F0.wireOp",EDGE,"E1.7.3.0"),sQuery(id+"F0.wireOp",EDGE,"E1.8.0.0"),sQuery(id+"F0.wireOp",EDGE,"E1.8.1.0"),sQuery(id+"F0.wireOp",EDGE,"E1.8.2.0"),sQuery(id+"F0.wireOp",EDGE,"E1.8.3.0"),sQuery(id+"F0.wireOp",EDGE,"E1.9.0.0"),sQuery(id+"F0.wireOp",EDGE,"E1.9.1.0"),sQuery(id+"F0.wireOp",EDGE,"E1.9.2.0"),sQuery(id+"F0.wireOp",EDGE,"E1.9.3.0"),sQuery(id+"F0.wireOp",EDGE,"E2.0.10.0"),sQuery(id+"F0.wireOp",EDGE,"E2.0.10.1"),sQuery(id+"F0.wireOp",EDGE,"E2.0.10.2"),sQuery(id+"F0.wireOp",EDGE,"E2.0.10.3"),sQuery(id+"F0.wireOp",EDGE,"E2.0.11.0"),sQuery(id+"F0.wireOp",EDGE,"E2.0.11.1"),sQuery(id+"F0.wireOp",EDGE,"E2.0.11.2"),sQuery(id+"F0.wireOp",EDGE,"E2.0.11.3"),sQuery(id+"F0.wireOp",EDGE,"E2.0.12.0"),sQuery(id+"F0.wireOp",EDGE,"E2.0.12.1"),sQuery(id+"F0.wireOp",EDGE,"E2.0.12.2"),sQuery(id+"F0.wireOp",EDGE,"E2.0.12.3"),sQuery(id+"F0.wireOp",EDGE,"E2.0.13.0"),sQuery(id+"F0.wireOp",EDGE,"E2.0.13.1"),sQuery(id+"F0.wireOp",EDGE,"E2.0.13.2"),sQuery(id+"F0.wireOp",EDGE,"E2.0.13.3"),sQuery(id+"F0.wireOp",EDGE,"E2.0.14.0"),sQuery(id+"F0.wireOp",EDGE,"E2.0.14.1"),sQuery(id+"F0.wireOp",EDGE,"E2.0.14.2"),sQuery(id+"F0.wireOp",EDGE,"E2.0.14.3"),sQuery(id+"F0.wireOp",EDGE,"E2.0.15.0"),sQuery(id+"F0.wireOp",EDGE,"E2.0.15.1"),sQuery(id+"F0.wireOp",EDGE,"E2.0.15.2"),sQuery(id+"F0.wireOp",EDGE,"E2.0.15.3"),sQuery(id+"F0.wireOp",EDGE,"E2.0.16.0"),sQuery(id+"F0.wireOp",EDGE,"E2.0.16.1"),sQuery(id+"F0.wireOp",EDGE,"E2.0.16.2"),sQuery(id+"F0.wireOp",EDGE,"E2.0.16.3"),sQuery(id+"F0.wireOp",EDGE,"E2.0.17.0"),sQuery(id+"F0.wireOp",EDGE,"E2.0.17.1"),sQuery(id+"F0.wireOp",EDGE,"E2.0.17.2"),sQuery(id+"F0.wireOp",EDGE,"E2.0.17.3"),sQuery(id+"F0.wireOp",EDGE,"E2.0.18.0"),sQuery(id+"F0.wireOp",EDGE,"E2.0.18.1"),sQuery(id+"F0.wireOp",EDGE,"E2.0.18.2"),sQuery(id+"F0.wireOp",EDGE,"E2.0.18.3"),sQuery(id+"F0.wireOp",EDGE,"E2.0.19.0"),sQuery(id+"F0.wireOp",EDGE,"E2.0.19.1"),sQuery(id+"F0.wireOp",EDGE,"E2.0.19.2"),sQuery(id+"F0.wireOp",EDGE,"E2.0.19.3"),sQuery(id+"F0.wireOp",EDGE,"E3.0.20.0"),sQuery(id+"F0.wireOp",EDGE,"E3.0.20.1"),sQuery(id+"F0.wireOp",EDGE,"E3.0.20.2"),sQuery(id+"F0.wireOp",EDGE,"E3.0.20.3"),sQuery(id+"F0.wireOp",EDGE,"E3.0.21.0"),sQuery(id+"F0.wireOp",EDGE,"E3.0.21.1"),sQuery(id+"F0.wireOp",EDGE,"E3.0.21.2"),sQuery(id+"F0.wireOp",EDGE,"E3.0.21.3"),sQuery(id+"F0.wireOp",EDGE,"E3.0.22.0"),sQuery(id+"F0.wireOp",EDGE,"E3.0.22.1"),sQuery(id+"F0.wireOp",EDGE,"E3.0.22.2"),sQuery(id+"F0.wireOp",EDGE,"E3.0.22.3"),sQuery(id+"F0.wireOp",EDGE,"E3.0.23.0"),sQuery(id+"F0.wireOp",EDGE,"E3.0.23.1"),sQuery(id+"F0.wireOp",EDGE,"E3.0.23.2"),sQuery(id+"F0.wireOp",EDGE,"E3.0.23.3"),sQuery(id+"F0.wireOp",EDGE,"E8"),sQuery(id+"F0.wireOp",EDGE,"E9.0.1.0"),sQuery(id+"F0.wireOp",EDGE,"E9.0.2.0"),sQuery(id+"F0.wireOp",EDGE,"E9.0.3.0"),sQuery(id+"F0.wireOp",EDGE,"E9.1.0.0"),sQuery(id+"F0.wireOp",EDGE,"E9.1.1.0"),sQuery(id+"F0.wireOp",EDGE,"E9.1.2.0"),sQuery(id+"F0.wireOp",EDGE,"E9.1.3.0"),sQuery(id+"F0.wireOp",EDGE,"E9.2.0.0"),sQuery(id+"F0.wireOp",EDGE,"E9.2.1.0"),sQuery(id+"F0.wireOp",EDGE,"E9.2.2.0"),sQuery(id+"F0.wireOp",EDGE,"E9.2.3.0"),sQuery(id+"F0.wireOp",EDGE,"E9.3.0.0"),sQuery(id+"F0.wireOp",EDGE,"E9.3.1.0"),sQuery(id+"F0.wireOp",EDGE,"E9.3.2.0"),sQuery(id+"F0.wireOp",EDGE,"E9.3.3.0"),sQuery(id+"F0.wireOp",EDGE,"E9.4.0.0"),sQuery(id+"F0.wireOp",EDGE,"E9.4.1.0"),sQuery(id+"F0.wireOp",EDGE,"E9.4.2.0"),sQuery(id+"F0.wireOp",EDGE,"E9.4.3.0"),sQuery(id+"F0.wireOp",EDGE,"E9.5.0.0"),sQuery(id+"F0.wireOp",EDGE,"E9.5.1.0"),sQuery(id+"F0.wireOp",EDGE,"E9.5.2.0"),sQuery(id+"F0.wireOp",EDGE,"E9.5.3.0"),sQuery(id+"F0.wireOp",EDGE,"E9.6.0.0"),sQuery(id+"F0.wireOp",EDGE,"E9.6.1.0"),sQuery(id+"F0.wireOp",EDGE,"E9.6.2.0"),sQuery(id+"F0.wireOp",EDGE,"E9.6.3.0"),sQuery(id+"F0.wireOp",EDGE,"E9.7.0.0"),sQuery(id+"F0.wireOp",EDGE,"E9.7.1.0"),sQuery(id+"F0.wireOp",EDGE,"E9.7.2.0"),sQuery(id+"F0.wireOp",EDGE,"E9.7.3.0"),sQuery(id+"F0.wireOp",EDGE,"E9.8.0.0"),sQuery(id+"F0.wireOp",EDGE,"E9.8.1.0"),sQuery(id+"F0.wireOp",EDGE,"E9.8.2.0"),sQuery(id+"F0.wireOp",EDGE,"E9.8.3.0"),sQuery(id+"F0.wireOp",EDGE,"E9.9.0.0"),sQuery(id+"F0.wireOp",EDGE,"E9.9.1.0"),sQuery(id+"F0.wireOp",EDGE,"E9.9.2.0"),sQuery(id+"F0.wireOp",EDGE,"E9.9.3.0"),sQuery(id+"F0.wireOp",EDGE,"E9.10.0.0"),sQuery(id+"F0.wireOp",EDGE,"E9.10.1.0"),sQuery(id+"F0.wireOp",EDGE,"E9.10.2.0"),sQuery(id+"F0.wireOp",EDGE,"E9.10.3.0"),sQuery(id+"F0.wireOp",EDGE,"E9.11.0.0"),sQuery(id+"F0.wireOp",EDGE,"E9.11.1.0"),sQuery(id+"F0.wireOp",EDGE,"E9.11.2.0"),sQuery(id+"F0.wireOp",EDGE,"E9.11.3.0"),sQuery(id+"F0.wireOp",EDGE,"E9.12.0.0"),sQuery(id+"F0.wireOp",EDGE,"E9.12.1.0"),sQuery(id+"F0.wireOp",EDGE,"E9.12.2.0"),sQuery(id+"F0.wireOp",EDGE,"E9.12.3.0"),sQuery(id+"F0.wireOp",EDGE,"E9.13.0.0"),sQuery(id+"F0.wireOp",EDGE,"E9.13.1.0"),sQuery(id+"F0.wireOp",EDGE,"E9.13.2.0"),sQuery(id+"F0.wireOp",EDGE,"E9.13.3.0"),sQuery(id+"F0.wireOp",EDGE,"E9.14.0.0"),sQuery(id+"F0.wireOp",EDGE,"E9.14.1.0"),sQuery(id+"F0.wireOp",EDGE,"E9.14.2.0"),sQuery(id+"F0.wireOp",EDGE,"E9.14.3.0"),sQuery(id+"F0.wireOp",EDGE,"E9.15.0.0"),sQuery(id+"F0.wireOp",EDGE,"E9.15.1.0"),sQuery(id+"F0.wireOp",EDGE,"E9.15.2.0"),sQuery(id+"F0.wireOp",EDGE,"E9.15.3.0"),sQuery(id+"F0.wireOp",EDGE,"E10.0"),sQuery(id+"F0.wireOp",EDGE,"E11.0"),sQuery(id+"F0.wireOp",EDGE,"E12.0"),sQuery(id+"F0.wireOp",EDGE,"E13.0"),sQuery(id+"F0.wireOp",EDGE,"E14.0"),sQuery(id+"F0.wireOp",EDGE,"E16"),sQuery(id+"F0.wireOp",EDGE,"E17"),sQuery(id+"F0.wireOp",EDGE,"E18"),sQuery(id+"F0.wireOp",EDGE,"E19"),sQuery(id+"F0.wireOp",EDGE,"E20"),sQuery(id+"F0.wireOp",EDGE,"E22"),sQuery(id+"F0.wireOp",EDGE,"E23"),sQuery(id+"F0.wireOp",EDGE,"E24")])],"isStart":false});
            var sketch = newSketch(context, id + "F7", { "sketchPlane" : qUnion([Q0]) });
            skArc(sketch, "E36.0", {"start": v(189.5, -64.59) * mm, "mid": v(188.6, -68.59) * mm, "end": v(189.5, -72.59) * mm});
            skArc(sketch, "E36.1", {"start": v(219.2, -116.03) * mm, "mid": v(218.3, -120.03) * mm, "end": v(219.2, -124.03) * mm});
            skLineSegment(sketch, "E37", {"start": v(198, -68.59) * mm, "end": v(495, -68.59) * mm, "construction": true});
            skLineSegment(sketch, "E38", {"start": v(198, -68.59) * mm, "end": v(227.7, -120.03) * mm, "construction": true});
            skLineSegment(sketch, "E39.0.left", {"start": v(198, -64.59) * mm, "end": v(495, -64.59) * mm});
            skLineSegment(sketch, "E39.0.right", {"start": v(198, -72.59) * mm, "end": v(495, -72.59) * mm});
            skLineSegment(sketch, "E40", {"start": v(198, -64.59) * mm, "end": v(189.5, -64.59) * mm});
            skLineSegment(sketch, "E41", {"start": v(198, -72.59) * mm, "end": v(189.5, -72.59) * mm});
            skLineSegment(sketch, "E42", {"start": v(495, -64.59) * mm, "end": v(503.5, -64.59) * mm});
            skLineSegment(sketch, "E43", {"start": v(495, -72.59) * mm, "end": v(503.5, -72.59) * mm});
            skArc(sketch, "E44.trimOffspring", {"start": v(503.5, -72.59) * mm, "mid": v(504.4, -68.59) * mm, "end": v(503.5, -64.59) * mm});
            skArc(sketch, "E45.0.1.0", {"start": v(199.4, -81.74) * mm, "mid": v(198.5, -85.74) * mm, "end": v(199.4, -89.74) * mm});
            skLineSegment(sketch, "E45.0.1.1", {"start": v(207.9, -81.74) * mm, "end": v(504.9, -81.74) * mm});
            skLineSegment(sketch, "E45.0.1.2", {"start": v(207.9, -89.74) * mm, "end": v(504.9, -89.74) * mm});
            skLineSegment(sketch, "E45.0.1.3", {"start": v(207.9, -81.74) * mm, "end": v(199.4, -81.74) * mm});
            skLineSegment(sketch, "E45.0.1.4", {"start": v(207.9, -89.74) * mm, "end": v(199.4, -89.74) * mm});
            skLineSegment(sketch, "E45.0.1.5", {"start": v(504.9, -81.74) * mm, "end": v(513.4, -81.74) * mm});
            skLineSegment(sketch, "E45.0.1.6", {"start": v(504.9, -89.74) * mm, "end": v(513.4, -89.74) * mm});
            skArc(sketch, "E45.0.1.7", {"start": v(513.4, -89.74) * mm, "mid": v(514.3, -85.74) * mm, "end": v(513.4, -81.74) * mm});
            skArc(sketch, "E45.0.2.0", {"start": v(209.3, -98.88) * mm, "mid": v(208.4, -102.88) * mm, "end": v(209.3, -106.88) * mm});
            skLineSegment(sketch, "E45.0.2.1", {"start": v(217.8, -98.88) * mm, "end": v(514.8, -98.88) * mm});
            skLineSegment(sketch, "E45.0.2.2", {"start": v(217.8, -106.88) * mm, "end": v(514.8, -106.88) * mm});
            skLineSegment(sketch, "E45.0.2.3", {"start": v(217.8, -98.88) * mm, "end": v(209.3, -98.88) * mm});
            skLineSegment(sketch, "E45.0.2.4", {"start": v(217.8, -106.88) * mm, "end": v(209.3, -106.88) * mm});
            skLineSegment(sketch, "E45.0.2.5", {"start": v(514.8, -98.88) * mm, "end": v(523.3, -98.88) * mm});
            skLineSegment(sketch, "E45.0.2.6", {"start": v(514.8, -106.88) * mm, "end": v(523.3, -106.88) * mm});
            skArc(sketch, "E45.0.2.7", {"start": v(523.3, -106.88) * mm, "mid": v(524.2, -102.88) * mm, "end": v(523.3, -98.88) * mm});
            skLineSegment(sketch, "E45.0.3.1", {"start": v(227.7, -116.03) * mm, "end": v(524.7, -116.03) * mm});
            skLineSegment(sketch, "E45.0.3.2", {"start": v(227.7, -124.03) * mm, "end": v(524.7, -124.03) * mm});
            skLineSegment(sketch, "E45.0.3.3", {"start": v(227.7, -116.03) * mm, "end": v(219.2, -116.03) * mm});
            skLineSegment(sketch, "E45.0.3.4", {"start": v(227.7, -124.03) * mm, "end": v(219.2, -124.03) * mm});
            skLineSegment(sketch, "E45.0.3.5", {"start": v(524.7, -116.03) * mm, "end": v(533.2, -116.03) * mm});
            skLineSegment(sketch, "E45.0.3.6", {"start": v(524.7, -124.03) * mm, "end": v(533.2, -124.03) * mm});
            skArc(sketch, "E45.0.3.7", {"start": v(533.2, -124.03) * mm, "mid": v(534.1, -120.03) * mm, "end": v(533.2, -116.03) * mm});
            skLineSegment(sketch, "E45.direction1", {"start": v(189.5, -72.59) * mm, "end": v(214.5, -72.59) * mm, "construction": true});
            skLineSegment(sketch, "E45.direction2", {"start": v(189.5, -72.59) * mm, "end": v(199.4, -89.74) * mm, "construction": true});
            skSolve(sketch);
        }
        {
            var Q0;
            Q0 = qSketchRegion(id + "F7", true);
            var Q1;
            Q1=makeQuery(id+"F4.opExtrude","CAP_FACE",FACE,{"disambiguationData":[OSD([sQuery(id+"F3.wireOp",EDGE,"E25.0"),sQuery(id+"F3.wireOp",EDGE,"E25.1"),sQuery(id+"F3.wireOp",EDGE,"E25.2"),sQuery(id+"F3.wireOp",EDGE,"E25.3"),sQuery(id+"F3.wireOp",EDGE,"E25.4"),sQuery(id+"F3.wireOp",EDGE,"E25.5"),sQuery(id+"F3.wireOp",EDGE,"E25.6"),sQuery(id+"F3.wireOp",EDGE,"E25.7"),sQuery(id+"F3.wireOp",EDGE,"E25.8"),sQuery(id+"F3.wireOp",EDGE,"E25.9"),sQuery(id+"F3.wireOp",EDGE,"E25.10"),sQuery(id+"F3.wireOp",EDGE,"E25.11")])],"isStart":false});
            extrude(context, id + "F8", {"entities" : qUnion([Q0]), "operationType" : NewBodyOperationType.REMOVE, "endBound" : BoundingType.UP_TO_SURFACE, "endBoundEntityFace" : qUnion([Q1]), "depth" : 25 * mm});
        }
        {
            var Q0;
            Q0=makeQuery(id+"F1.opExtrude","CAP_FACE",FACE,{"disambiguationData":[OSD([sQuery(id+"F0.wireOp",EDGE,"E0"),sQuery(id+"F0.wireOp",EDGE,"E1.0.1.0"),sQuery(id+"F0.wireOp",EDGE,"E1.0.2.0"),sQuery(id+"F0.wireOp",EDGE,"E1.0.3.0"),sQuery(id+"F0.wireOp",EDGE,"E1.1.0.0"),sQuery(id+"F0.wireOp",EDGE,"E1.1.1.0"),sQuery(id+"F0.wireOp",EDGE,"E1.1.2.0"),sQuery(id+"F0.wireOp",EDGE,"E1.1.3.0"),sQuery(id+"F0.wireOp",EDGE,"E1.2.0.0"),sQuery(id+"F0.wireOp",EDGE,"E1.2.1.0"),sQuery(id+"F0.wireOp",EDGE,"E1.2.2.0"),sQuery(id+"F0.wireOp",EDGE,"E1.2.3.0"),sQuery(id+"F0.wireOp",EDGE,"E1.3.0.0"),sQuery(id+"F0.wireOp",EDGE,"E1.3.1.0"),sQuery(id+"F0.wireOp",EDGE,"E1.3.2.0"),sQuery(id+"F0.wireOp",EDGE,"E1.3.3.0"),sQuery(id+"F0.wireOp",EDGE,"E1.4.0.0"),sQuery(id+"F0.wireOp",EDGE,"E1.4.1.0"),sQuery(id+"F0.wireOp",EDGE,"E1.4.2.0"),sQuery(id+"F0.wireOp",EDGE,"E1.4.3.0"),sQuery(id+"F0.wireOp",EDGE,"E1.5.0.0"),sQuery(id+"F0.wireOp",EDGE,"E1.5.1.0"),sQuery(id+"F0.wireOp",EDGE,"E1.5.2.0"),sQuery(id+"F0.wireOp",EDGE,"E1.5.3.0"),sQuery(id+"F0.wireOp",EDGE,"E1.6.0.0"),sQuery(id+"F0.wireOp",EDGE,"E1.6.1.0"),sQuery(id+"F0.wireOp",EDGE,"E1.6.2.0"),sQuery(id+"F0.wireOp",EDGE,"E1.6.3.0"),sQuery(id+"F0.wireOp",EDGE,"E1.7.0.0"),sQuery(id+"F0.wireOp",EDGE,"E1.7.1.0"),sQuery(id+"F0.wireOp",EDGE,"E1.7.2.0"),sQuery(id+"F0.wireOp",EDGE,"E1.7.3.0"),sQuery(id+"F0.wireOp",EDGE,"E1.8.0.0"),sQuery(id+"F0.wireOp",EDGE,"E1.8.1.0"),sQuery(id+"F0.wireOp",EDGE,"E1.8.2.0"),sQuery(id+"F0.wireOp",EDGE,"E1.8.3.0"),sQuery(id+"F0.wireOp",EDGE,"E1.9.0.0"),sQuery(id+"F0.wireOp",EDGE,"E1.9.1.0"),sQuery(id+"F0.wireOp",EDGE,"E1.9.2.0"),sQuery(id+"F0.wireOp",EDGE,"E1.9.3.0"),sQuery(id+"F0.wireOp",EDGE,"E2.0.10.0"),sQuery(id+"F0.wireOp",EDGE,"E2.0.10.1"),sQuery(id+"F0.wireOp",EDGE,"E2.0.10.2"),sQuery(id+"F0.wireOp",EDGE,"E2.0.10.3"),sQuery(id+"F0.wireOp",EDGE,"E2.0.11.0"),sQuery(id+"F0.wireOp",EDGE,"E2.0.11.1"),sQuery(id+"F0.wireOp",EDGE,"E2.0.11.2"),sQuery(id+"F0.wireOp",EDGE,"E2.0.11.3"),sQuery(id+"F0.wireOp",EDGE,"E2.0.12.0"),sQuery(id+"F0.wireOp",EDGE,"E2.0.12.1"),sQuery(id+"F0.wireOp",EDGE,"E2.0.12.2"),sQuery(id+"F0.wireOp",EDGE,"E2.0.12.3"),sQuery(id+"F0.wireOp",EDGE,"E2.0.13.0"),sQuery(id+"F0.wireOp",EDGE,"E2.0.13.1"),sQuery(id+"F0.wireOp",EDGE,"E2.0.13.2"),sQuery(id+"F0.wireOp",EDGE,"E2.0.13.3"),sQuery(id+"F0.wireOp",EDGE,"E2.0.14.0"),sQuery(id+"F0.wireOp",EDGE,"E2.0.14.1"),sQuery(id+"F0.wireOp",EDGE,"E2.0.14.2"),sQuery(id+"F0.wireOp",EDGE,"E2.0.14.3"),sQuery(id+"F0.wireOp",EDGE,"E2.0.15.0"),sQuery(id+"F0.wireOp",EDGE,"E2.0.15.1"),sQuery(id+"F0.wireOp",EDGE,"E2.0.15.2"),sQuery(id+"F0.wireOp",EDGE,"E2.0.15.3"),sQuery(id+"F0.wireOp",EDGE,"E2.0.16.0"),sQuery(id+"F0.wireOp",EDGE,"E2.0.16.1"),sQuery(id+"F0.wireOp",EDGE,"E2.0.16.2"),sQuery(id+"F0.wireOp",EDGE,"E2.0.16.3"),sQuery(id+"F0.wireOp",EDGE,"E2.0.17.0"),sQuery(id+"F0.wireOp",EDGE,"E2.0.17.1"),sQuery(id+"F0.wireOp",EDGE,"E2.0.17.2"),sQuery(id+"F0.wireOp",EDGE,"E2.0.17.3"),sQuery(id+"F0.wireOp",EDGE,"E2.0.18.0"),sQuery(id+"F0.wireOp",EDGE,"E2.0.18.1"),sQuery(id+"F0.wireOp",EDGE,"E2.0.18.2"),sQuery(id+"F0.wireOp",EDGE,"E2.0.18.3"),sQuery(id+"F0.wireOp",EDGE,"E2.0.19.0"),sQuery(id+"F0.wireOp",EDGE,"E2.0.19.1"),sQuery(id+"F0.wireOp",EDGE,"E2.0.19.2"),sQuery(id+"F0.wireOp",EDGE,"E2.0.19.3"),sQuery(id+"F0.wireOp",EDGE,"E3.0.20.0"),sQuery(id+"F0.wireOp",EDGE,"E3.0.20.1"),sQuery(id+"F0.wireOp",EDGE,"E3.0.20.2"),sQuery(id+"F0.wireOp",EDGE,"E3.0.20.3"),sQuery(id+"F0.wireOp",EDGE,"E3.0.21.0"),sQuery(id+"F0.wireOp",EDGE,"E3.0.21.1"),sQuery(id+"F0.wireOp",EDGE,"E3.0.21.2"),sQuery(id+"F0.wireOp",EDGE,"E3.0.21.3"),sQuery(id+"F0.wireOp",EDGE,"E3.0.22.0"),sQuery(id+"F0.wireOp",EDGE,"E3.0.22.1"),sQuery(id+"F0.wireOp",EDGE,"E3.0.22.2"),sQuery(id+"F0.wireOp",EDGE,"E3.0.22.3"),sQuery(id+"F0.wireOp",EDGE,"E3.0.23.0"),sQuery(id+"F0.wireOp",EDGE,"E3.0.23.1"),sQuery(id+"F0.wireOp",EDGE,"E3.0.23.2"),sQuery(id+"F0.wireOp",EDGE,"E3.0.23.3"),sQuery(id+"F0.wireOp",EDGE,"E8"),sQuery(id+"F0.wireOp",EDGE,"E9.0.1.0"),sQuery(id+"F0.wireOp",EDGE,"E9.0.2.0"),sQuery(id+"F0.wireOp",EDGE,"E9.0.3.0"),sQuery(id+"F0.wireOp",EDGE,"E9.1.0.0"),sQuery(id+"F0.wireOp",EDGE,"E9.1.1.0"),sQuery(id+"F0.wireOp",EDGE,"E9.1.2.0"),sQuery(id+"F0.wireOp",EDGE,"E9.1.3.0"),sQuery(id+"F0.wireOp",EDGE,"E9.2.0.0"),sQuery(id+"F0.wireOp",EDGE,"E9.2.1.0"),sQuery(id+"F0.wireOp",EDGE,"E9.2.2.0"),sQuery(id+"F0.wireOp",EDGE,"E9.2.3.0"),sQuery(id+"F0.wireOp",EDGE,"E9.3.0.0"),sQuery(id+"F0.wireOp",EDGE,"E9.3.1.0"),sQuery(id+"F0.wireOp",EDGE,"E9.3.2.0"),sQuery(id+"F0.wireOp",EDGE,"E9.3.3.0"),sQuery(id+"F0.wireOp",EDGE,"E9.4.0.0"),sQuery(id+"F0.wireOp",EDGE,"E9.4.1.0"),sQuery(id+"F0.wireOp",EDGE,"E9.4.2.0"),sQuery(id+"F0.wireOp",EDGE,"E9.4.3.0"),sQuery(id+"F0.wireOp",EDGE,"E9.5.0.0"),sQuery(id+"F0.wireOp",EDGE,"E9.5.1.0"),sQuery(id+"F0.wireOp",EDGE,"E9.5.2.0"),sQuery(id+"F0.wireOp",EDGE,"E9.5.3.0"),sQuery(id+"F0.wireOp",EDGE,"E9.6.0.0"),sQuery(id+"F0.wireOp",EDGE,"E9.6.1.0"),sQuery(id+"F0.wireOp",EDGE,"E9.6.2.0"),sQuery(id+"F0.wireOp",EDGE,"E9.6.3.0"),sQuery(id+"F0.wireOp",EDGE,"E9.7.0.0"),sQuery(id+"F0.wireOp",EDGE,"E9.7.1.0"),sQuery(id+"F0.wireOp",EDGE,"E9.7.2.0"),sQuery(id+"F0.wireOp",EDGE,"E9.7.3.0"),sQuery(id+"F0.wireOp",EDGE,"E9.8.0.0"),sQuery(id+"F0.wireOp",EDGE,"E9.8.1.0"),sQuery(id+"F0.wireOp",EDGE,"E9.8.2.0"),sQuery(id+"F0.wireOp",EDGE,"E9.8.3.0"),sQuery(id+"F0.wireOp",EDGE,"E9.9.0.0"),sQuery(id+"F0.wireOp",EDGE,"E9.9.1.0"),sQuery(id+"F0.wireOp",EDGE,"E9.9.2.0"),sQuery(id+"F0.wireOp",EDGE,"E9.9.3.0"),sQuery(id+"F0.wireOp",EDGE,"E9.10.0.0"),sQuery(id+"F0.wireOp",EDGE,"E9.10.1.0"),sQuery(id+"F0.wireOp",EDGE,"E9.10.2.0"),sQuery(id+"F0.wireOp",EDGE,"E9.10.3.0"),sQuery(id+"F0.wireOp",EDGE,"E9.11.0.0"),sQuery(id+"F0.wireOp",EDGE,"E9.11.1.0"),sQuery(id+"F0.wireOp",EDGE,"E9.11.2.0"),sQuery(id+"F0.wireOp",EDGE,"E9.11.3.0"),sQuery(id+"F0.wireOp",EDGE,"E9.12.0.0"),sQuery(id+"F0.wireOp",EDGE,"E9.12.1.0"),sQuery(id+"F0.wireOp",EDGE,"E9.12.2.0"),sQuery(id+"F0.wireOp",EDGE,"E9.12.3.0"),sQuery(id+"F0.wireOp",EDGE,"E9.13.0.0"),sQuery(id+"F0.wireOp",EDGE,"E9.13.1.0"),sQuery(id+"F0.wireOp",EDGE,"E9.13.2.0"),sQuery(id+"F0.wireOp",EDGE,"E9.13.3.0"),sQuery(id+"F0.wireOp",EDGE,"E9.14.0.0"),sQuery(id+"F0.wireOp",EDGE,"E9.14.1.0"),sQuery(id+"F0.wireOp",EDGE,"E9.14.2.0"),sQuery(id+"F0.wireOp",EDGE,"E9.14.3.0"),sQuery(id+"F0.wireOp",EDGE,"E9.15.0.0"),sQuery(id+"F0.wireOp",EDGE,"E9.15.1.0"),sQuery(id+"F0.wireOp",EDGE,"E9.15.2.0"),sQuery(id+"F0.wireOp",EDGE,"E9.15.3.0"),sQuery(id+"F0.wireOp",EDGE,"E10.0"),sQuery(id+"F0.wireOp",EDGE,"E11.0"),sQuery(id+"F0.wireOp",EDGE,"E12.0"),sQuery(id+"F0.wireOp",EDGE,"E13.0"),sQuery(id+"F0.wireOp",EDGE,"E14.0"),sQuery(id+"F0.wireOp",EDGE,"E16"),sQuery(id+"F0.wireOp",EDGE,"E17"),sQuery(id+"F0.wireOp",EDGE,"E18"),sQuery(id+"F0.wireOp",EDGE,"E19"),sQuery(id+"F0.wireOp",EDGE,"E20"),sQuery(id+"F0.wireOp",EDGE,"E22"),sQuery(id+"F0.wireOp",EDGE,"E23"),sQuery(id+"F0.wireOp",EDGE,"E24")])],"isStart":false});
            var sketch = newSketch(context, id + "F9", { "sketchPlane" : qUnion([Q0]) });
            skArc(sketch, "E46.0", {"start": v(-0.79, 9.37) * mm, "mid": v(-4.7, 8.14) * mm, "end": v(-7.72, 5.37) * mm});
            skArc(sketch, "E46.1", {"start": v(30.49, -60.8) * mm, "mid": v(34.4, -59.58) * mm, "end": v(37.42, -56.8) * mm});
            skLineSegment(sketch, "E47", {"start": v(0, 0) * mm, "end": v(29.7, -51.44) * mm, "construction": true});
            skLineSegment(sketch, "E48.0.left", {"start": v(3.46, 2) * mm, "end": v(33.16, -49.44) * mm});
            skLineSegment(sketch, "E48.0.right", {"start": v(-3.46, -2) * mm, "end": v(26.24, -53.44) * mm});
            skLineSegment(sketch, "E49", {"start": v(3.46, 2) * mm, "end": v(-0.79, 9.37) * mm});
            skLineSegment(sketch, "E50", {"start": v(-3.46, -2) * mm, "end": v(-7.72, 5.37) * mm});
            skLineSegment(sketch, "E51", {"start": v(26.24, -53.44) * mm, "end": v(30.49, -60.8) * mm});
            skLineSegment(sketch, "E52", {"start": v(33.16, -49.44) * mm, "end": v(37.42, -56.8) * mm});
            skArc(sketch, "E53.1.0.0", {"start": v(19.01, 9.37) * mm, "mid": v(15.1, 8.14) * mm, "end": v(12.08, 5.37) * mm});
            skLineSegment(sketch, "E53.1.0.1", {"start": v(16.34, -2) * mm, "end": v(12.08, 5.37) * mm});
            skLineSegment(sketch, "E53.1.0.2", {"start": v(23.26, 2) * mm, "end": v(19.01, 9.37) * mm});
            skLineSegment(sketch, "E53.1.0.3", {"start": v(23.26, 2) * mm, "end": v(52.96, -49.44) * mm});
            skLineSegment(sketch, "E53.1.0.4", {"start": v(16.34, -2) * mm, "end": v(46.04, -53.44) * mm});
            skLineSegment(sketch, "E53.1.0.5", {"start": v(46.04, -53.44) * mm, "end": v(50.29, -60.8) * mm});
            skLineSegment(sketch, "E53.1.0.6", {"start": v(52.96, -49.44) * mm, "end": v(57.22, -56.8) * mm});
            skArc(sketch, "E53.1.0.7", {"start": v(50.29, -60.8) * mm, "mid": v(54.2, -59.58) * mm, "end": v(57.22, -56.8) * mm});
            skArc(sketch, "E53.2.0.0", {"start": v(38.81, 9.37) * mm, "mid": v(34.9, 8.14) * mm, "end": v(31.88, 5.37) * mm});
            skLineSegment(sketch, "E53.2.0.1", {"start": v(36.14, -2) * mm, "end": v(31.88, 5.37) * mm});
            skLineSegment(sketch, "E53.2.0.2", {"start": v(43.06, 2) * mm, "end": v(38.81, 9.37) * mm});
            skLineSegment(sketch, "E53.2.0.3", {"start": v(43.06, 2) * mm, "end": v(72.76, -49.44) * mm});
            skLineSegment(sketch, "E53.2.0.4", {"start": v(36.14, -2) * mm, "end": v(65.84, -53.44) * mm});
            skLineSegment(sketch, "E53.2.0.5", {"start": v(65.84, -53.44) * mm, "end": v(70.09, -60.8) * mm});
            skLineSegment(sketch, "E53.2.0.6", {"start": v(72.76, -49.44) * mm, "end": v(77.02, -56.8) * mm});
            skArc(sketch, "E53.2.0.7", {"start": v(70.09, -60.8) * mm, "mid": v(74, -59.58) * mm, "end": v(77.02, -56.8) * mm});
            skArc(sketch, "E53.3.0.0", {"start": v(58.61, 9.37) * mm, "mid": v(54.7, 8.14) * mm, "end": v(51.68, 5.37) * mm});
            skLineSegment(sketch, "E53.3.0.1", {"start": v(55.94, -2) * mm, "end": v(51.68, 5.37) * mm});
            skLineSegment(sketch, "E53.3.0.2", {"start": v(62.86, 2) * mm, "end": v(58.61, 9.37) * mm});
            skLineSegment(sketch, "E53.3.0.3", {"start": v(62.86, 2) * mm, "end": v(92.56, -49.44) * mm});
            skLineSegment(sketch, "E53.3.0.4", {"start": v(55.94, -2) * mm, "end": v(85.64, -53.44) * mm});
            skLineSegment(sketch, "E53.3.0.5", {"start": v(85.64, -53.44) * mm, "end": v(89.89, -60.8) * mm});
            skLineSegment(sketch, "E53.3.0.6", {"start": v(92.56, -49.44) * mm, "end": v(96.82, -56.8) * mm});
            skArc(sketch, "E53.3.0.7", {"start": v(89.89, -60.8) * mm, "mid": v(93.8, -59.58) * mm, "end": v(96.82, -56.8) * mm});
            skArc(sketch, "E53.4.0.0", {"start": v(78.41, 9.37) * mm, "mid": v(74.5, 8.14) * mm, "end": v(71.48, 5.37) * mm});
            skLineSegment(sketch, "E53.4.0.1", {"start": v(75.74, -2) * mm, "end": v(71.48, 5.37) * mm});
            skLineSegment(sketch, "E53.4.0.2", {"start": v(82.66, 2) * mm, "end": v(78.41, 9.37) * mm});
            skLineSegment(sketch, "E53.4.0.3", {"start": v(82.66, 2) * mm, "end": v(112.36, -49.44) * mm});
            skLineSegment(sketch, "E53.4.0.4", {"start": v(75.74, -2) * mm, "end": v(105.44, -53.44) * mm});
            skLineSegment(sketch, "E53.4.0.5", {"start": v(105.44, -53.44) * mm, "end": v(109.69, -60.8) * mm});
            skLineSegment(sketch, "E53.4.0.6", {"start": v(112.36, -49.44) * mm, "end": v(116.62, -56.8) * mm});
            skArc(sketch, "E53.4.0.7", {"start": v(109.69, -60.8) * mm, "mid": v(113.6, -59.58) * mm, "end": v(116.62, -56.8) * mm});
            skArc(sketch, "E53.5.0.0", {"start": v(98.21, 9.37) * mm, "mid": v(94.3, 8.14) * mm, "end": v(91.28, 5.37) * mm});
            skLineSegment(sketch, "E53.5.0.1", {"start": v(95.54, -2) * mm, "end": v(91.28, 5.37) * mm});
            skLineSegment(sketch, "E53.5.0.2", {"start": v(102.46, 2) * mm, "end": v(98.21, 9.37) * mm});
            skLineSegment(sketch, "E53.5.0.3", {"start": v(102.46, 2) * mm, "end": v(132.16, -49.44) * mm});
            skLineSegment(sketch, "E53.5.0.4", {"start": v(95.54, -2) * mm, "end": v(125.24, -53.44) * mm});
            skLineSegment(sketch, "E53.5.0.5", {"start": v(125.24, -53.44) * mm, "end": v(129.49, -60.8) * mm});
            skLineSegment(sketch, "E53.5.0.6", {"start": v(132.16, -49.44) * mm, "end": v(136.42, -56.8) * mm});
            skArc(sketch, "E53.5.0.7", {"start": v(129.49, -60.8) * mm, "mid": v(133.4, -59.58) * mm, "end": v(136.42, -56.8) * mm});
            skArc(sketch, "E53.6.0.0", {"start": v(118.01, 9.37) * mm, "mid": v(114.1, 8.14) * mm, "end": v(111.08, 5.37) * mm});
            skLineSegment(sketch, "E53.6.0.1", {"start": v(115.34, -2) * mm, "end": v(111.08, 5.37) * mm});
            skLineSegment(sketch, "E53.6.0.2", {"start": v(122.26, 2) * mm, "end": v(118.01, 9.37) * mm});
            skLineSegment(sketch, "E53.6.0.3", {"start": v(122.26, 2) * mm, "end": v(151.96, -49.44) * mm});
            skLineSegment(sketch, "E53.6.0.4", {"start": v(115.34, -2) * mm, "end": v(145.04, -53.44) * mm});
            skLineSegment(sketch, "E53.6.0.5", {"start": v(145.04, -53.44) * mm, "end": v(149.29, -60.8) * mm});
            skLineSegment(sketch, "E53.6.0.6", {"start": v(151.96, -49.44) * mm, "end": v(156.22, -56.8) * mm});
            skArc(sketch, "E53.6.0.7", {"start": v(149.29, -60.8) * mm, "mid": v(153.2, -59.58) * mm, "end": v(156.22, -56.8) * mm});
            skArc(sketch, "E53.7.0.0", {"start": v(137.81, 9.37) * mm, "mid": v(133.9, 8.14) * mm, "end": v(130.88, 5.37) * mm});
            skLineSegment(sketch, "E53.7.0.1", {"start": v(135.14, -2) * mm, "end": v(130.88, 5.37) * mm});
            skLineSegment(sketch, "E53.7.0.2", {"start": v(142.06, 2) * mm, "end": v(137.81, 9.37) * mm});
            skLineSegment(sketch, "E53.7.0.3", {"start": v(142.06, 2) * mm, "end": v(171.76, -49.44) * mm});
            skLineSegment(sketch, "E53.7.0.4", {"start": v(135.14, -2) * mm, "end": v(164.84, -53.44) * mm});
            skLineSegment(sketch, "E53.7.0.5", {"start": v(164.84, -53.44) * mm, "end": v(169.09, -60.8) * mm});
            skLineSegment(sketch, "E53.7.0.6", {"start": v(171.76, -49.44) * mm, "end": v(176.02, -56.8) * mm});
            skArc(sketch, "E53.7.0.7", {"start": v(169.09, -60.8) * mm, "mid": v(173, -59.58) * mm, "end": v(176.02, -56.8) * mm});
            skLineSegment(sketch, "E53.direction1", {"start": v(-7.72, 5.37) * mm, "end": v(12.08, 5.37) * mm, "construction": true});
            skSolve(sketch);
        }
        {
            var Q0;
            Q0 = qSketchRegion(id + "F9", true);
            var Q1;
            Q1=makeQuery(id+"F4.opExtrude","CAP_FACE",FACE,{"disambiguationData":[OSD([sQuery(id+"F3.wireOp",EDGE,"E25.0"),sQuery(id+"F3.wireOp",EDGE,"E25.1"),sQuery(id+"F3.wireOp",EDGE,"E25.2"),sQuery(id+"F3.wireOp",EDGE,"E25.3"),sQuery(id+"F3.wireOp",EDGE,"E25.4"),sQuery(id+"F3.wireOp",EDGE,"E25.5"),sQuery(id+"F3.wireOp",EDGE,"E25.6"),sQuery(id+"F3.wireOp",EDGE,"E25.7"),sQuery(id+"F3.wireOp",EDGE,"E25.8"),sQuery(id+"F3.wireOp",EDGE,"E25.9"),sQuery(id+"F3.wireOp",EDGE,"E25.10"),sQuery(id+"F3.wireOp",EDGE,"E25.11")])],"isStart":false});
            extrude(context, id + "F10", {"entities" : qUnion([Q0]), "operationType" : NewBodyOperationType.REMOVE, "endBound" : BoundingType.UP_TO_SURFACE, "endBoundEntityFace" : qUnion([Q1]), "depth" : 25 * mm});
        }
        {
            var Q0;
            Q0=makeQuery(id+"F1.opExtrude","CAP_FACE",FACE,{"disambiguationData":[OSD([sQuery(id+"F0.wireOp",EDGE,"E0"),sQuery(id+"F0.wireOp",EDGE,"E1.0.1.0"),sQuery(id+"F0.wireOp",EDGE,"E1.0.2.0"),sQuery(id+"F0.wireOp",EDGE,"E1.0.3.0"),sQuery(id+"F0.wireOp",EDGE,"E1.1.0.0"),sQuery(id+"F0.wireOp",EDGE,"E1.1.1.0"),sQuery(id+"F0.wireOp",EDGE,"E1.1.2.0"),sQuery(id+"F0.wireOp",EDGE,"E1.1.3.0"),sQuery(id+"F0.wireOp",EDGE,"E1.2.0.0"),sQuery(id+"F0.wireOp",EDGE,"E1.2.1.0"),sQuery(id+"F0.wireOp",EDGE,"E1.2.2.0"),sQuery(id+"F0.wireOp",EDGE,"E1.2.3.0"),sQuery(id+"F0.wireOp",EDGE,"E1.3.0.0"),sQuery(id+"F0.wireOp",EDGE,"E1.3.1.0"),sQuery(id+"F0.wireOp",EDGE,"E1.3.2.0"),sQuery(id+"F0.wireOp",EDGE,"E1.3.3.0"),sQuery(id+"F0.wireOp",EDGE,"E1.4.0.0"),sQuery(id+"F0.wireOp",EDGE,"E1.4.1.0"),sQuery(id+"F0.wireOp",EDGE,"E1.4.2.0"),sQuery(id+"F0.wireOp",EDGE,"E1.4.3.0"),sQuery(id+"F0.wireOp",EDGE,"E1.5.0.0"),sQuery(id+"F0.wireOp",EDGE,"E1.5.1.0"),sQuery(id+"F0.wireOp",EDGE,"E1.5.2.0"),sQuery(id+"F0.wireOp",EDGE,"E1.5.3.0"),sQuery(id+"F0.wireOp",EDGE,"E1.6.0.0"),sQuery(id+"F0.wireOp",EDGE,"E1.6.1.0"),sQuery(id+"F0.wireOp",EDGE,"E1.6.2.0"),sQuery(id+"F0.wireOp",EDGE,"E1.6.3.0"),sQuery(id+"F0.wireOp",EDGE,"E1.7.0.0"),sQuery(id+"F0.wireOp",EDGE,"E1.7.1.0"),sQuery(id+"F0.wireOp",EDGE,"E1.7.2.0"),sQuery(id+"F0.wireOp",EDGE,"E1.7.3.0"),sQuery(id+"F0.wireOp",EDGE,"E1.8.0.0"),sQuery(id+"F0.wireOp",EDGE,"E1.8.1.0"),sQuery(id+"F0.wireOp",EDGE,"E1.8.2.0"),sQuery(id+"F0.wireOp",EDGE,"E1.8.3.0"),sQuery(id+"F0.wireOp",EDGE,"E1.9.0.0"),sQuery(id+"F0.wireOp",EDGE,"E1.9.1.0"),sQuery(id+"F0.wireOp",EDGE,"E1.9.2.0"),sQuery(id+"F0.wireOp",EDGE,"E1.9.3.0"),sQuery(id+"F0.wireOp",EDGE,"E2.0.10.0"),sQuery(id+"F0.wireOp",EDGE,"E2.0.10.1"),sQuery(id+"F0.wireOp",EDGE,"E2.0.10.2"),sQuery(id+"F0.wireOp",EDGE,"E2.0.10.3"),sQuery(id+"F0.wireOp",EDGE,"E2.0.11.0"),sQuery(id+"F0.wireOp",EDGE,"E2.0.11.1"),sQuery(id+"F0.wireOp",EDGE,"E2.0.11.2"),sQuery(id+"F0.wireOp",EDGE,"E2.0.11.3"),sQuery(id+"F0.wireOp",EDGE,"E2.0.12.0"),sQuery(id+"F0.wireOp",EDGE,"E2.0.12.1"),sQuery(id+"F0.wireOp",EDGE,"E2.0.12.2"),sQuery(id+"F0.wireOp",EDGE,"E2.0.12.3"),sQuery(id+"F0.wireOp",EDGE,"E2.0.13.0"),sQuery(id+"F0.wireOp",EDGE,"E2.0.13.1"),sQuery(id+"F0.wireOp",EDGE,"E2.0.13.2"),sQuery(id+"F0.wireOp",EDGE,"E2.0.13.3"),sQuery(id+"F0.wireOp",EDGE,"E2.0.14.0"),sQuery(id+"F0.wireOp",EDGE,"E2.0.14.1"),sQuery(id+"F0.wireOp",EDGE,"E2.0.14.2"),sQuery(id+"F0.wireOp",EDGE,"E2.0.14.3"),sQuery(id+"F0.wireOp",EDGE,"E2.0.15.0"),sQuery(id+"F0.wireOp",EDGE,"E2.0.15.1"),sQuery(id+"F0.wireOp",EDGE,"E2.0.15.2"),sQuery(id+"F0.wireOp",EDGE,"E2.0.15.3"),sQuery(id+"F0.wireOp",EDGE,"E2.0.16.0"),sQuery(id+"F0.wireOp",EDGE,"E2.0.16.1"),sQuery(id+"F0.wireOp",EDGE,"E2.0.16.2"),sQuery(id+"F0.wireOp",EDGE,"E2.0.16.3"),sQuery(id+"F0.wireOp",EDGE,"E2.0.17.0"),sQuery(id+"F0.wireOp",EDGE,"E2.0.17.1"),sQuery(id+"F0.wireOp",EDGE,"E2.0.17.2"),sQuery(id+"F0.wireOp",EDGE,"E2.0.17.3"),sQuery(id+"F0.wireOp",EDGE,"E2.0.18.0"),sQuery(id+"F0.wireOp",EDGE,"E2.0.18.1"),sQuery(id+"F0.wireOp",EDGE,"E2.0.18.2"),sQuery(id+"F0.wireOp",EDGE,"E2.0.18.3"),sQuery(id+"F0.wireOp",EDGE,"E2.0.19.0"),sQuery(id+"F0.wireOp",EDGE,"E2.0.19.1"),sQuery(id+"F0.wireOp",EDGE,"E2.0.19.2"),sQuery(id+"F0.wireOp",EDGE,"E2.0.19.3"),sQuery(id+"F0.wireOp",EDGE,"E3.0.20.0"),sQuery(id+"F0.wireOp",EDGE,"E3.0.20.1"),sQuery(id+"F0.wireOp",EDGE,"E3.0.20.2"),sQuery(id+"F0.wireOp",EDGE,"E3.0.20.3"),sQuery(id+"F0.wireOp",EDGE,"E3.0.21.0"),sQuery(id+"F0.wireOp",EDGE,"E3.0.21.1"),sQuery(id+"F0.wireOp",EDGE,"E3.0.21.2"),sQuery(id+"F0.wireOp",EDGE,"E3.0.21.3"),sQuery(id+"F0.wireOp",EDGE,"E3.0.22.0"),sQuery(id+"F0.wireOp",EDGE,"E3.0.22.1"),sQuery(id+"F0.wireOp",EDGE,"E3.0.22.2"),sQuery(id+"F0.wireOp",EDGE,"E3.0.22.3"),sQuery(id+"F0.wireOp",EDGE,"E3.0.23.0"),sQuery(id+"F0.wireOp",EDGE,"E3.0.23.1"),sQuery(id+"F0.wireOp",EDGE,"E3.0.23.2"),sQuery(id+"F0.wireOp",EDGE,"E3.0.23.3"),sQuery(id+"F0.wireOp",EDGE,"E8"),sQuery(id+"F0.wireOp",EDGE,"E9.0.1.0"),sQuery(id+"F0.wireOp",EDGE,"E9.0.2.0"),sQuery(id+"F0.wireOp",EDGE,"E9.0.3.0"),sQuery(id+"F0.wireOp",EDGE,"E9.1.0.0"),sQuery(id+"F0.wireOp",EDGE,"E9.1.1.0"),sQuery(id+"F0.wireOp",EDGE,"E9.1.2.0"),sQuery(id+"F0.wireOp",EDGE,"E9.1.3.0"),sQuery(id+"F0.wireOp",EDGE,"E9.2.0.0"),sQuery(id+"F0.wireOp",EDGE,"E9.2.1.0"),sQuery(id+"F0.wireOp",EDGE,"E9.2.2.0"),sQuery(id+"F0.wireOp",EDGE,"E9.2.3.0"),sQuery(id+"F0.wireOp",EDGE,"E9.3.0.0"),sQuery(id+"F0.wireOp",EDGE,"E9.3.1.0"),sQuery(id+"F0.wireOp",EDGE,"E9.3.2.0"),sQuery(id+"F0.wireOp",EDGE,"E9.3.3.0"),sQuery(id+"F0.wireOp",EDGE,"E9.4.0.0"),sQuery(id+"F0.wireOp",EDGE,"E9.4.1.0"),sQuery(id+"F0.wireOp",EDGE,"E9.4.2.0"),sQuery(id+"F0.wireOp",EDGE,"E9.4.3.0"),sQuery(id+"F0.wireOp",EDGE,"E9.5.0.0"),sQuery(id+"F0.wireOp",EDGE,"E9.5.1.0"),sQuery(id+"F0.wireOp",EDGE,"E9.5.2.0"),sQuery(id+"F0.wireOp",EDGE,"E9.5.3.0"),sQuery(id+"F0.wireOp",EDGE,"E9.6.0.0"),sQuery(id+"F0.wireOp",EDGE,"E9.6.1.0"),sQuery(id+"F0.wireOp",EDGE,"E9.6.2.0"),sQuery(id+"F0.wireOp",EDGE,"E9.6.3.0"),sQuery(id+"F0.wireOp",EDGE,"E9.7.0.0"),sQuery(id+"F0.wireOp",EDGE,"E9.7.1.0"),sQuery(id+"F0.wireOp",EDGE,"E9.7.2.0"),sQuery(id+"F0.wireOp",EDGE,"E9.7.3.0"),sQuery(id+"F0.wireOp",EDGE,"E9.8.0.0"),sQuery(id+"F0.wireOp",EDGE,"E9.8.1.0"),sQuery(id+"F0.wireOp",EDGE,"E9.8.2.0"),sQuery(id+"F0.wireOp",EDGE,"E9.8.3.0"),sQuery(id+"F0.wireOp",EDGE,"E9.9.0.0"),sQuery(id+"F0.wireOp",EDGE,"E9.9.1.0"),sQuery(id+"F0.wireOp",EDGE,"E9.9.2.0"),sQuery(id+"F0.wireOp",EDGE,"E9.9.3.0"),sQuery(id+"F0.wireOp",EDGE,"E9.10.0.0"),sQuery(id+"F0.wireOp",EDGE,"E9.10.1.0"),sQuery(id+"F0.wireOp",EDGE,"E9.10.2.0"),sQuery(id+"F0.wireOp",EDGE,"E9.10.3.0"),sQuery(id+"F0.wireOp",EDGE,"E9.11.0.0"),sQuery(id+"F0.wireOp",EDGE,"E9.11.1.0"),sQuery(id+"F0.wireOp",EDGE,"E9.11.2.0"),sQuery(id+"F0.wireOp",EDGE,"E9.11.3.0"),sQuery(id+"F0.wireOp",EDGE,"E9.12.0.0"),sQuery(id+"F0.wireOp",EDGE,"E9.12.1.0"),sQuery(id+"F0.wireOp",EDGE,"E9.12.2.0"),sQuery(id+"F0.wireOp",EDGE,"E9.12.3.0"),sQuery(id+"F0.wireOp",EDGE,"E9.13.0.0"),sQuery(id+"F0.wireOp",EDGE,"E9.13.1.0"),sQuery(id+"F0.wireOp",EDGE,"E9.13.2.0"),sQuery(id+"F0.wireOp",EDGE,"E9.13.3.0"),sQuery(id+"F0.wireOp",EDGE,"E9.14.0.0"),sQuery(id+"F0.wireOp",EDGE,"E9.14.1.0"),sQuery(id+"F0.wireOp",EDGE,"E9.14.2.0"),sQuery(id+"F0.wireOp",EDGE,"E9.14.3.0"),sQuery(id+"F0.wireOp",EDGE,"E9.15.0.0"),sQuery(id+"F0.wireOp",EDGE,"E9.15.1.0"),sQuery(id+"F0.wireOp",EDGE,"E9.15.2.0"),sQuery(id+"F0.wireOp",EDGE,"E9.15.3.0"),sQuery(id+"F0.wireOp",EDGE,"E10.0"),sQuery(id+"F0.wireOp",EDGE,"E11.0"),sQuery(id+"F0.wireOp",EDGE,"E12.0"),sQuery(id+"F0.wireOp",EDGE,"E13.0"),sQuery(id+"F0.wireOp",EDGE,"E14.0"),sQuery(id+"F0.wireOp",EDGE,"E16"),sQuery(id+"F0.wireOp",EDGE,"E17"),sQuery(id+"F0.wireOp",EDGE,"E18"),sQuery(id+"F0.wireOp",EDGE,"E19"),sQuery(id+"F0.wireOp",EDGE,"E20"),sQuery(id+"F0.wireOp",EDGE,"E22"),sQuery(id+"F0.wireOp",EDGE,"E23"),sQuery(id+"F0.wireOp",EDGE,"E24")])],"isStart":false});
            var sketch = newSketch(context, id + "F11", { "sketchPlane" : qUnion([Q0]) });
            skArc(sketch, "E54.0", {"start": v(157.61, 9.37) * mm, "mid": v(153.7, 8.14) * mm, "end": v(150.68, 5.37) * mm});
            skArc(sketch, "E54.1", {"start": v(228.49, -129.4) * mm, "mid": v(232.4, -128.17) * mm, "end": v(235.42, -125.4) * mm});
            skLineSegment(sketch, "E55", {"start": v(158.4, 0) * mm, "end": v(227.7, -120.03) * mm, "construction": true});
            skLineSegment(sketch, "E56.0.left", {"start": v(161.86, 2) * mm, "end": v(231.16, -118.03) * mm});
            skLineSegment(sketch, "E56.0.right", {"start": v(154.94, -2) * mm, "end": v(224.24, -122.03) * mm});
            skLineSegment(sketch, "E57", {"start": v(161.86, 2) * mm, "end": v(157.61, 9.37) * mm});
            skLineSegment(sketch, "E58", {"start": v(154.94, -2) * mm, "end": v(150.68, 5.37) * mm});
            skLineSegment(sketch, "E59", {"start": v(224.24, -122.03) * mm, "end": v(228.49, -129.4) * mm});
            skLineSegment(sketch, "E60", {"start": v(231.16, -118.03) * mm, "end": v(235.42, -125.4) * mm});
            skArc(sketch, "E61.1.0.0", {"start": v(177.41, 9.37) * mm, "mid": v(173.5, 8.14) * mm, "end": v(170.48, 5.37) * mm});
            skLineSegment(sketch, "E61.1.0.1", {"start": v(174.74, -2) * mm, "end": v(170.48, 5.37) * mm});
            skLineSegment(sketch, "E61.1.0.2", {"start": v(181.66, 2) * mm, "end": v(177.41, 9.37) * mm});
            skLineSegment(sketch, "E61.1.0.3", {"start": v(181.66, 2) * mm, "end": v(250.96, -118.03) * mm});
            skLineSegment(sketch, "E61.1.0.4", {"start": v(174.74, -2) * mm, "end": v(244.04, -122.03) * mm});
            skLineSegment(sketch, "E61.1.0.5", {"start": v(244.04, -122.03) * mm, "end": v(248.29, -129.4) * mm});
            skLineSegment(sketch, "E61.1.0.6", {"start": v(250.96, -118.03) * mm, "end": v(255.22, -125.4) * mm});
            skArc(sketch, "E61.1.0.7", {"start": v(248.29, -129.4) * mm, "mid": v(252.2, -128.17) * mm, "end": v(255.22, -125.4) * mm});
            skArc(sketch, "E61.2.0.0", {"start": v(197.21, 9.37) * mm, "mid": v(193.3, 8.14) * mm, "end": v(190.28, 5.37) * mm});
            skLineSegment(sketch, "E61.2.0.1", {"start": v(194.54, -2) * mm, "end": v(190.28, 5.37) * mm});
            skLineSegment(sketch, "E61.2.0.2", {"start": v(201.46, 2) * mm, "end": v(197.21, 9.37) * mm});
            skLineSegment(sketch, "E61.2.0.3", {"start": v(201.46, 2) * mm, "end": v(270.76, -118.03) * mm});
            skLineSegment(sketch, "E61.2.0.4", {"start": v(194.54, -2) * mm, "end": v(263.84, -122.03) * mm});
            skLineSegment(sketch, "E61.2.0.5", {"start": v(263.84, -122.03) * mm, "end": v(268.09, -129.4) * mm});
            skLineSegment(sketch, "E61.2.0.6", {"start": v(270.76, -118.03) * mm, "end": v(275.02, -125.4) * mm});
            skArc(sketch, "E61.2.0.7", {"start": v(268.09, -129.4) * mm, "mid": v(272, -128.17) * mm, "end": v(275.02, -125.4) * mm});
            skArc(sketch, "E61.3.0.0", {"start": v(217.01, 9.37) * mm, "mid": v(213.1, 8.14) * mm, "end": v(210.08, 5.37) * mm});
            skLineSegment(sketch, "E61.3.0.1", {"start": v(214.34, -2) * mm, "end": v(210.08, 5.37) * mm});
            skLineSegment(sketch, "E61.3.0.2", {"start": v(221.26, 2) * mm, "end": v(217.01, 9.37) * mm});
            skLineSegment(sketch, "E61.3.0.3", {"start": v(221.26, 2) * mm, "end": v(290.56, -118.03) * mm});
            skLineSegment(sketch, "E61.3.0.4", {"start": v(214.34, -2) * mm, "end": v(283.64, -122.03) * mm});
            skLineSegment(sketch, "E61.3.0.5", {"start": v(283.64, -122.03) * mm, "end": v(287.89, -129.4) * mm});
            skLineSegment(sketch, "E61.3.0.6", {"start": v(290.56, -118.03) * mm, "end": v(294.82, -125.4) * mm});
            skArc(sketch, "E61.3.0.7", {"start": v(287.89, -129.4) * mm, "mid": v(291.8, -128.17) * mm, "end": v(294.82, -125.4) * mm});
            skArc(sketch, "E61.4.0.0", {"start": v(236.81, 9.37) * mm, "mid": v(232.9, 8.14) * mm, "end": v(229.88, 5.37) * mm});
            skLineSegment(sketch, "E61.4.0.1", {"start": v(234.14, -2) * mm, "end": v(229.88, 5.37) * mm});
            skLineSegment(sketch, "E61.4.0.2", {"start": v(241.06, 2) * mm, "end": v(236.81, 9.37) * mm});
            skLineSegment(sketch, "E61.4.0.3", {"start": v(241.06, 2) * mm, "end": v(310.36, -118.03) * mm});
            skLineSegment(sketch, "E61.4.0.4", {"start": v(234.14, -2) * mm, "end": v(303.44, -122.03) * mm});
            skLineSegment(sketch, "E61.4.0.5", {"start": v(303.44, -122.03) * mm, "end": v(307.69, -129.4) * mm});
            skLineSegment(sketch, "E61.4.0.6", {"start": v(310.36, -118.03) * mm, "end": v(314.62, -125.4) * mm});
            skArc(sketch, "E61.4.0.7", {"start": v(307.69, -129.4) * mm, "mid": v(311.6, -128.17) * mm, "end": v(314.62, -125.4) * mm});
            skArc(sketch, "E61.5.0.0", {"start": v(256.61, 9.37) * mm, "mid": v(252.7, 8.14) * mm, "end": v(249.68, 5.37) * mm});
            skLineSegment(sketch, "E61.5.0.1", {"start": v(253.94, -2) * mm, "end": v(249.68, 5.37) * mm});
            skLineSegment(sketch, "E61.5.0.2", {"start": v(260.86, 2) * mm, "end": v(256.61, 9.37) * mm});
            skLineSegment(sketch, "E61.5.0.3", {"start": v(260.86, 2) * mm, "end": v(330.16, -118.03) * mm});
            skLineSegment(sketch, "E61.5.0.4", {"start": v(253.94, -2) * mm, "end": v(323.24, -122.03) * mm});
            skLineSegment(sketch, "E61.5.0.5", {"start": v(323.24, -122.03) * mm, "end": v(327.49, -129.4) * mm});
            skLineSegment(sketch, "E61.5.0.6", {"start": v(330.16, -118.03) * mm, "end": v(334.42, -125.4) * mm});
            skArc(sketch, "E61.5.0.7", {"start": v(327.49, -129.4) * mm, "mid": v(331.4, -128.17) * mm, "end": v(334.42, -125.4) * mm});
            skArc(sketch, "E61.6.0.0", {"start": v(276.41, 9.37) * mm, "mid": v(272.5, 8.14) * mm, "end": v(269.48, 5.37) * mm});
            skLineSegment(sketch, "E61.6.0.1", {"start": v(273.74, -2) * mm, "end": v(269.48, 5.37) * mm});
            skLineSegment(sketch, "E61.6.0.2", {"start": v(280.66, 2) * mm, "end": v(276.41, 9.37) * mm});
            skLineSegment(sketch, "E61.6.0.3", {"start": v(280.66, 2) * mm, "end": v(349.96, -118.03) * mm});
            skLineSegment(sketch, "E61.6.0.4", {"start": v(273.74, -2) * mm, "end": v(343.04, -122.03) * mm});
            skLineSegment(sketch, "E61.6.0.5", {"start": v(343.04, -122.03) * mm, "end": v(347.29, -129.4) * mm});
            skLineSegment(sketch, "E61.6.0.6", {"start": v(349.96, -118.03) * mm, "end": v(354.22, -125.4) * mm});
            skArc(sketch, "E61.6.0.7", {"start": v(347.29, -129.4) * mm, "mid": v(351.2, -128.17) * mm, "end": v(354.22, -125.4) * mm});
            skArc(sketch, "E61.7.0.0", {"start": v(296.21, 9.37) * mm, "mid": v(292.3, 8.14) * mm, "end": v(289.28, 5.37) * mm});
            skLineSegment(sketch, "E61.7.0.1", {"start": v(293.54, -2) * mm, "end": v(289.28, 5.37) * mm});
            skLineSegment(sketch, "E61.7.0.2", {"start": v(300.46, 2) * mm, "end": v(296.21, 9.37) * mm});
            skLineSegment(sketch, "E61.7.0.3", {"start": v(300.46, 2) * mm, "end": v(369.76, -118.03) * mm});
            skLineSegment(sketch, "E61.7.0.4", {"start": v(293.54, -2) * mm, "end": v(362.84, -122.03) * mm});
            skLineSegment(sketch, "E61.7.0.5", {"start": v(362.84, -122.03) * mm, "end": v(367.09, -129.4) * mm});
            skLineSegment(sketch, "E61.7.0.6", {"start": v(369.76, -118.03) * mm, "end": v(374.02, -125.4) * mm});
            skArc(sketch, "E61.7.0.7", {"start": v(367.09, -129.4) * mm, "mid": v(371, -128.17) * mm, "end": v(374.02, -125.4) * mm});
            skArc(sketch, "E61.8.0.0", {"start": v(316.01, 9.37) * mm, "mid": v(312.1, 8.14) * mm, "end": v(309.08, 5.37) * mm});
            skLineSegment(sketch, "E61.8.0.1", {"start": v(313.34, -2) * mm, "end": v(309.08, 5.37) * mm});
            skLineSegment(sketch, "E61.8.0.2", {"start": v(320.26, 2) * mm, "end": v(316.01, 9.37) * mm});
            skLineSegment(sketch, "E61.8.0.3", {"start": v(320.26, 2) * mm, "end": v(389.56, -118.03) * mm});
            skLineSegment(sketch, "E61.8.0.4", {"start": v(313.34, -2) * mm, "end": v(382.64, -122.03) * mm});
            skLineSegment(sketch, "E61.8.0.5", {"start": v(382.64, -122.03) * mm, "end": v(386.89, -129.4) * mm});
            skLineSegment(sketch, "E61.8.0.6", {"start": v(389.56, -118.03) * mm, "end": v(393.82, -125.4) * mm});
            skArc(sketch, "E61.8.0.7", {"start": v(386.89, -129.4) * mm, "mid": v(390.8, -128.17) * mm, "end": v(393.82, -125.4) * mm});
            skArc(sketch, "E61.9.0.0", {"start": v(335.81, 9.37) * mm, "mid": v(331.9, 8.14) * mm, "end": v(328.88, 5.37) * mm});
            skLineSegment(sketch, "E61.9.0.1", {"start": v(333.14, -2) * mm, "end": v(328.88, 5.37) * mm});
            skLineSegment(sketch, "E61.9.0.2", {"start": v(340.06, 2) * mm, "end": v(335.81, 9.37) * mm});
            skLineSegment(sketch, "E61.9.0.3", {"start": v(340.06, 2) * mm, "end": v(409.36, -118.03) * mm});
            skLineSegment(sketch, "E61.9.0.4", {"start": v(333.14, -2) * mm, "end": v(402.44, -122.03) * mm});
            skLineSegment(sketch, "E61.9.0.5", {"start": v(402.44, -122.03) * mm, "end": v(406.69, -129.4) * mm});
            skLineSegment(sketch, "E61.9.0.6", {"start": v(409.36, -118.03) * mm, "end": v(413.62, -125.4) * mm});
            skArc(sketch, "E61.9.0.7", {"start": v(406.69, -129.4) * mm, "mid": v(410.6, -128.17) * mm, "end": v(413.62, -125.4) * mm});
            skArc(sketch, "E61.10.0.0", {"start": v(355.61, 9.37) * mm, "mid": v(351.7, 8.14) * mm, "end": v(348.68, 5.37) * mm});
            skLineSegment(sketch, "E61.10.0.1", {"start": v(352.94, -2) * mm, "end": v(348.68, 5.37) * mm});
            skLineSegment(sketch, "E61.10.0.2", {"start": v(359.86, 2) * mm, "end": v(355.61, 9.37) * mm});
            skLineSegment(sketch, "E61.10.0.3", {"start": v(359.86, 2) * mm, "end": v(429.16, -118.03) * mm});
            skLineSegment(sketch, "E61.10.0.4", {"start": v(352.94, -2) * mm, "end": v(422.24, -122.03) * mm});
            skLineSegment(sketch, "E61.10.0.5", {"start": v(422.24, -122.03) * mm, "end": v(426.49, -129.4) * mm});
            skLineSegment(sketch, "E61.10.0.6", {"start": v(429.16, -118.03) * mm, "end": v(433.42, -125.4) * mm});
            skArc(sketch, "E61.10.0.7", {"start": v(426.49, -129.4) * mm, "mid": v(430.4, -128.17) * mm, "end": v(433.42, -125.4) * mm});
            skArc(sketch, "E61.11.0.0", {"start": v(375.41, 9.37) * mm, "mid": v(371.5, 8.14) * mm, "end": v(368.48, 5.37) * mm});
            skLineSegment(sketch, "E61.11.0.1", {"start": v(372.74, -2) * mm, "end": v(368.48, 5.37) * mm});
            skLineSegment(sketch, "E61.11.0.2", {"start": v(379.66, 2) * mm, "end": v(375.41, 9.37) * mm});
            skLineSegment(sketch, "E61.11.0.3", {"start": v(379.66, 2) * mm, "end": v(448.96, -118.03) * mm});
            skLineSegment(sketch, "E61.11.0.4", {"start": v(372.74, -2) * mm, "end": v(442.04, -122.03) * mm});
            skLineSegment(sketch, "E61.11.0.5", {"start": v(442.04, -122.03) * mm, "end": v(446.29, -129.4) * mm});
            skLineSegment(sketch, "E61.11.0.6", {"start": v(448.96, -118.03) * mm, "end": v(453.22, -125.4) * mm});
            skArc(sketch, "E61.11.0.7", {"start": v(446.29, -129.4) * mm, "mid": v(450.2, -128.17) * mm, "end": v(453.22, -125.4) * mm});
            skArc(sketch, "E61.12.0.0", {"start": v(395.21, 9.37) * mm, "mid": v(391.3, 8.14) * mm, "end": v(388.28, 5.37) * mm});
            skLineSegment(sketch, "E61.12.0.1", {"start": v(392.54, -2) * mm, "end": v(388.28, 5.37) * mm});
            skLineSegment(sketch, "E61.12.0.2", {"start": v(399.46, 2) * mm, "end": v(395.21, 9.37) * mm});
            skLineSegment(sketch, "E61.12.0.3", {"start": v(399.46, 2) * mm, "end": v(468.76, -118.03) * mm});
            skLineSegment(sketch, "E61.12.0.4", {"start": v(392.54, -2) * mm, "end": v(461.84, -122.03) * mm});
            skLineSegment(sketch, "E61.12.0.5", {"start": v(461.84, -122.03) * mm, "end": v(466.09, -129.4) * mm});
            skLineSegment(sketch, "E61.12.0.6", {"start": v(468.76, -118.03) * mm, "end": v(473.02, -125.4) * mm});
            skArc(sketch, "E61.12.0.7", {"start": v(466.09, -129.4) * mm, "mid": v(470, -128.17) * mm, "end": v(473.02, -125.4) * mm});
            skArc(sketch, "E61.13.0.0", {"start": v(415.01, 9.37) * mm, "mid": v(411.1, 8.14) * mm, "end": v(408.08, 5.37) * mm});
            skLineSegment(sketch, "E61.13.0.1", {"start": v(412.34, -2) * mm, "end": v(408.08, 5.37) * mm});
            skLineSegment(sketch, "E61.13.0.2", {"start": v(419.26, 2) * mm, "end": v(415.01, 9.37) * mm});
            skLineSegment(sketch, "E61.13.0.3", {"start": v(419.26, 2) * mm, "end": v(488.56, -118.03) * mm});
            skLineSegment(sketch, "E61.13.0.4", {"start": v(412.34, -2) * mm, "end": v(481.64, -122.03) * mm});
            skLineSegment(sketch, "E61.13.0.5", {"start": v(481.64, -122.03) * mm, "end": v(485.89, -129.4) * mm});
            skLineSegment(sketch, "E61.13.0.6", {"start": v(488.56, -118.03) * mm, "end": v(492.82, -125.4) * mm});
            skArc(sketch, "E61.13.0.7", {"start": v(485.89, -129.4) * mm, "mid": v(489.8, -128.17) * mm, "end": v(492.82, -125.4) * mm});
            skArc(sketch, "E61.14.0.0", {"start": v(434.81, 9.37) * mm, "mid": v(430.9, 8.14) * mm, "end": v(427.88, 5.37) * mm});
            skLineSegment(sketch, "E61.14.0.1", {"start": v(432.14, -2) * mm, "end": v(427.88, 5.37) * mm});
            skLineSegment(sketch, "E61.14.0.2", {"start": v(439.06, 2) * mm, "end": v(434.81, 9.37) * mm});
            skLineSegment(sketch, "E61.14.0.3", {"start": v(439.06, 2) * mm, "end": v(508.36, -118.03) * mm});
            skLineSegment(sketch, "E61.14.0.4", {"start": v(432.14, -2) * mm, "end": v(501.44, -122.03) * mm});
            skLineSegment(sketch, "E61.14.0.5", {"start": v(501.44, -122.03) * mm, "end": v(505.69, -129.4) * mm});
            skLineSegment(sketch, "E61.14.0.6", {"start": v(508.36, -118.03) * mm, "end": v(512.62, -125.4) * mm});
            skArc(sketch, "E61.14.0.7", {"start": v(505.69, -129.4) * mm, "mid": v(509.6, -128.17) * mm, "end": v(512.62, -125.4) * mm});
            skArc(sketch, "E61.15.0.0", {"start": v(454.61, 9.37) * mm, "mid": v(450.7, 8.14) * mm, "end": v(447.68, 5.37) * mm});
            skLineSegment(sketch, "E61.15.0.1", {"start": v(451.94, -2) * mm, "end": v(447.68, 5.37) * mm});
            skLineSegment(sketch, "E61.15.0.2", {"start": v(458.86, 2) * mm, "end": v(454.61, 9.37) * mm});
            skLineSegment(sketch, "E61.15.0.3", {"start": v(458.86, 2) * mm, "end": v(528.16, -118.03) * mm});
            skLineSegment(sketch, "E61.15.0.4", {"start": v(451.94, -2) * mm, "end": v(521.24, -122.03) * mm});
            skLineSegment(sketch, "E61.15.0.5", {"start": v(521.24, -122.03) * mm, "end": v(525.49, -129.4) * mm});
            skLineSegment(sketch, "E61.15.0.6", {"start": v(528.16, -118.03) * mm, "end": v(532.42, -125.4) * mm});
            skArc(sketch, "E61.15.0.7", {"start": v(525.49, -129.4) * mm, "mid": v(529.4, -128.17) * mm, "end": v(532.42, -125.4) * mm});
            skLineSegment(sketch, "E61.direction1", {"start": v(150.68, 5.37) * mm, "end": v(170.48, 5.37) * mm, "construction": true});
            skSolve(sketch);
        }
        {
            var Q0;
            Q0 = qSketchRegion(id + "F11", true);
            var Q1;
            {var subQ0=sQuery(id+"F3.wireOp",EDGE,"E25.0");var subQ1=sQuery(id+"F3.wireOp",EDGE,"E25.3");var subQ2=sQuery(id+"F3.wireOp",EDGE,"E25.1");var subQ3=sQuery(id+"F3.wireOp",EDGE,"E25.2");var subQ4=sQuery(id+"F3.wireOp",EDGE,"E25.4");var subQ5=sQuery(id+"F3.wireOp",EDGE,"E25.5");var subQ6=sQuery(id+"F3.wireOp",EDGE,"E25.6");var subQ7=sQuery(id+"F3.wireOp",EDGE,"E25.7");var subQ8=sQuery(id+"F3.wireOp",EDGE,"E25.8");var subQ9=sQuery(id+"F3.wireOp",EDGE,"E25.9");var subQ10=sQuery(id+"F3.wireOp",EDGE,"E25.10");var subQ11=sQuery(id+"F3.wireOp",EDGE,"E25.11");Q1=makeQuery(id+"F10.boolean.opBoolean","SPLIT",FACE,{"disambiguationData":[TD([makeQuery(id+"F4.opExtrude","SWEPT_FACE",FACE,{"disambiguationData":[OSD([subQ0])]}),makeQuery(id+"F4.opExtrude","SWEPT_FACE",FACE,{"disambiguationData":[OSD([subQ2])]}),makeQuery(id+"F4.opExtrude","SWEPT_FACE",FACE,{"disambiguationData":[OSD([subQ3])]}),makeQuery(id+"F4.opExtrude","SWEPT_FACE",FACE,{"disambiguationData":[OSD([subQ1])]}),makeQuery(id+"F4.opExtrude","SWEPT_FACE",FACE,{"disambiguationData":[OSD([subQ4])]}),makeQuery(id+"F4.opExtrude","SWEPT_FACE",FACE,{"disambiguationData":[OSD([subQ5])]}),makeQuery(id+"F4.opExtrude","SWEPT_FACE",FACE,{"disambiguationData":[OSD([subQ6])]}),makeQuery(id+"F4.opExtrude","SWEPT_FACE",FACE,{"disambiguationData":[OSD([subQ7])]}),makeQuery(id+"F4.opExtrude","SWEPT_FACE",FACE,{"disambiguationData":[OSD([subQ8])]}),makeQuery(id+"F4.opExtrude","SWEPT_FACE",FACE,{"disambiguationData":[OSD([subQ9])]}),makeQuery(id+"F4.opExtrude","SWEPT_FACE",FACE,{"disambiguationData":[OSD([subQ10])]}),makeQuery(id+"F4.opExtrude","SWEPT_FACE",FACE,{"disambiguationData":[OSD([subQ11])]}),makeQuery(id+"F6.boolean.opBoolean","COPY",FACE,{"derivedFrom":makeQuery(id+"F6.opExtrude","SWEPT_FACE",FACE,{"disambiguationData":[OSD([sQuery(id+"F5.wireOp",EDGE,"E26.0")])]})}),makeQuery(id+"F6.boolean.opBoolean","COPY",FACE,{"derivedFrom":makeQuery(id+"F6.opExtrude","SWEPT_FACE",FACE,{"disambiguationData":[OSD([sQuery(id+"F5.wireOp",EDGE,"E31.0.left"),sQuery(id+"F5.wireOp",EDGE,"E32")])]})}),makeQuery(id+"F6.boolean.opBoolean","COPY",FACE,{"derivedFrom":makeQuery(id+"F6.opExtrude","SWEPT_FACE",FACE,{"disambiguationData":[OSD([sQuery(id+"F5.wireOp",EDGE,"E31.0.right"),sQuery(id+"F5.wireOp",EDGE,"E33")])]})}),makeQuery(id+"F6.boolean.opBoolean","COPY",FACE,{"derivedFrom":makeQuery(id+"F6.opExtrude","SWEPT_FACE",FACE,{"disambiguationData":[OSD([sQuery(id+"F5.wireOp",EDGE,"E34.trimOffspring")])]})}),makeQuery(id+"F6.boolean.opBoolean","COPY",FACE,{"derivedFrom":makeQuery(id+"F6.opExtrude","SWEPT_FACE",FACE,{"disambiguationData":[OSD([sQuery(id+"F5.wireOp",EDGE,"E35.0.1.0")])]})}),makeQuery(id+"F6.boolean.opBoolean","COPY",FACE,{"derivedFrom":makeQuery(id+"F6.opExtrude","SWEPT_FACE",FACE,{"disambiguationData":[OSD([sQuery(id+"F5.wireOp",EDGE,"E35.0.1.1"),sQuery(id+"F5.wireOp",EDGE,"E35.0.1.3")])]})}),makeQuery(id+"F6.boolean.opBoolean","COPY",FACE,{"derivedFrom":makeQuery(id+"F6.opExtrude","SWEPT_FACE",FACE,{"disambiguationData":[OSD([sQuery(id+"F5.wireOp",EDGE,"E35.0.1.2"),sQuery(id+"F5.wireOp",EDGE,"E35.0.1.4")])]})}),makeQuery(id+"F6.boolean.opBoolean","COPY",FACE,{"derivedFrom":makeQuery(id+"F6.opExtrude","SWEPT_FACE",FACE,{"disambiguationData":[OSD([sQuery(id+"F5.wireOp",EDGE,"E35.0.1.5")])]})}),makeQuery(id+"F6.boolean.opBoolean","COPY",FACE,{"derivedFrom":makeQuery(id+"F6.opExtrude","SWEPT_FACE",FACE,{"disambiguationData":[OSD([sQuery(id+"F5.wireOp",EDGE,"E35.0.2.0")])]})}),makeQuery(id+"F6.boolean.opBoolean","COPY",FACE,{"derivedFrom":makeQuery(id+"F6.opExtrude","SWEPT_FACE",FACE,{"disambiguationData":[OSD([sQuery(id+"F5.wireOp",EDGE,"E35.0.2.1"),sQuery(id+"F5.wireOp",EDGE,"E35.0.2.3")])]})}),makeQuery(id+"F6.boolean.opBoolean","COPY",FACE,{"derivedFrom":makeQuery(id+"F6.opExtrude","SWEPT_FACE",FACE,{"disambiguationData":[OSD([sQuery(id+"F5.wireOp",EDGE,"E35.0.2.2"),sQuery(id+"F5.wireOp",EDGE,"E35.0.2.4")])]})}),makeQuery(id+"F6.boolean.opBoolean","COPY",FACE,{"derivedFrom":makeQuery(id+"F6.opExtrude","SWEPT_FACE",FACE,{"disambiguationData":[OSD([sQuery(id+"F5.wireOp",EDGE,"E35.0.2.5")])]})}),makeQuery(id+"F6.boolean.opBoolean","COPY",FACE,{"derivedFrom":makeQuery(id+"F6.opExtrude","SWEPT_FACE",FACE,{"disambiguationData":[OSD([sQuery(id+"F5.wireOp",EDGE,"E26.1")])]})}),makeQuery(id+"F6.boolean.opBoolean","COPY",FACE,{"derivedFrom":makeQuery(id+"F6.opExtrude","SWEPT_FACE",FACE,{"disambiguationData":[OSD([sQuery(id+"F5.wireOp",EDGE,"E35.0.3.1"),sQuery(id+"F5.wireOp",EDGE,"E35.0.3.3")])]})}),makeQuery(id+"F6.boolean.opBoolean","COPY",FACE,{"derivedFrom":makeQuery(id+"F6.opExtrude","SWEPT_FACE",FACE,{"disambiguationData":[OSD([sQuery(id+"F5.wireOp",EDGE,"E35.0.3.2"),sQuery(id+"F5.wireOp",EDGE,"E35.0.3.4")])]})}),makeQuery(id+"F6.boolean.opBoolean","COPY",FACE,{"derivedFrom":makeQuery(id+"F6.opExtrude","SWEPT_FACE",FACE,{"disambiguationData":[OSD([sQuery(id+"F5.wireOp",EDGE,"E35.0.3.5")])]})}),makeQuery(id+"F8.boolean.opBoolean","COPY",FACE,{"derivedFrom":makeQuery(id+"F8.opExtrude","SWEPT_FACE",FACE,{"disambiguationData":[OSD([sQuery(id+"F7.wireOp",EDGE,"E36.0")])]})}),makeQuery(id+"F8.boolean.opBoolean","COPY",FACE,{"derivedFrom":makeQuery(id+"F8.opExtrude","SWEPT_FACE",FACE,{"disambiguationData":[OSD([sQuery(id+"F7.wireOp",EDGE,"E39.0.left"),sQuery(id+"F7.wireOp",EDGE,"E40"),sQuery(id+"F7.wireOp",EDGE,"E42")])]})}),makeQuery(id+"F8.boolean.opBoolean","COPY",FACE,{"derivedFrom":makeQuery(id+"F8.opExtrude","SWEPT_FACE",FACE,{"disambiguationData":[OSD([sQuery(id+"F7.wireOp",EDGE,"E39.0.right"),sQuery(id+"F7.wireOp",EDGE,"E41"),sQuery(id+"F7.wireOp",EDGE,"E43")])]})}),makeQuery(id+"F8.boolean.opBoolean","COPY",FACE,{"derivedFrom":makeQuery(id+"F8.opExtrude","SWEPT_FACE",FACE,{"disambiguationData":[OSD([sQuery(id+"F7.wireOp",EDGE,"E44.trimOffspring")])]})}),makeQuery(id+"F8.boolean.opBoolean","COPY",FACE,{"derivedFrom":makeQuery(id+"F8.opExtrude","SWEPT_FACE",FACE,{"disambiguationData":[OSD([sQuery(id+"F7.wireOp",EDGE,"E45.0.1.0")])]})}),makeQuery(id+"F8.boolean.opBoolean","COPY",FACE,{"derivedFrom":makeQuery(id+"F8.opExtrude","SWEPT_FACE",FACE,{"disambiguationData":[OSD([sQuery(id+"F7.wireOp",EDGE,"E45.0.1.1"),sQuery(id+"F7.wireOp",EDGE,"E45.0.1.3"),sQuery(id+"F7.wireOp",EDGE,"E45.0.1.5")])]})}),makeQuery(id+"F8.boolean.opBoolean","COPY",FACE,{"derivedFrom":makeQuery(id+"F8.opExtrude","SWEPT_FACE",FACE,{"disambiguationData":[OSD([sQuery(id+"F7.wireOp",EDGE,"E45.0.1.2"),sQuery(id+"F7.wireOp",EDGE,"E45.0.1.4"),sQuery(id+"F7.wireOp",EDGE,"E45.0.1.6")])]})}),makeQuery(id+"F8.boolean.opBoolean","COPY",FACE,{"derivedFrom":makeQuery(id+"F8.opExtrude","SWEPT_FACE",FACE,{"disambiguationData":[OSD([sQuery(id+"F7.wireOp",EDGE,"E45.0.1.7")])]})}),makeQuery(id+"F8.boolean.opBoolean","COPY",FACE,{"derivedFrom":makeQuery(id+"F8.opExtrude","SWEPT_FACE",FACE,{"disambiguationData":[OSD([sQuery(id+"F7.wireOp",EDGE,"E45.0.2.0")])]})}),makeQuery(id+"F8.boolean.opBoolean","COPY",FACE,{"derivedFrom":makeQuery(id+"F8.opExtrude","SWEPT_FACE",FACE,{"disambiguationData":[OSD([sQuery(id+"F7.wireOp",EDGE,"E45.0.2.1"),sQuery(id+"F7.wireOp",EDGE,"E45.0.2.3"),sQuery(id+"F7.wireOp",EDGE,"E45.0.2.5")])]})}),makeQuery(id+"F8.boolean.opBoolean","COPY",FACE,{"derivedFrom":makeQuery(id+"F8.opExtrude","SWEPT_FACE",FACE,{"disambiguationData":[OSD([sQuery(id+"F7.wireOp",EDGE,"E45.0.2.2"),sQuery(id+"F7.wireOp",EDGE,"E45.0.2.4"),sQuery(id+"F7.wireOp",EDGE,"E45.0.2.6")])]})}),makeQuery(id+"F8.boolean.opBoolean","COPY",FACE,{"derivedFrom":makeQuery(id+"F8.opExtrude","SWEPT_FACE",FACE,{"disambiguationData":[OSD([sQuery(id+"F7.wireOp",EDGE,"E45.0.2.7")])]})}),makeQuery(id+"F8.boolean.opBoolean","COPY",FACE,{"derivedFrom":makeQuery(id+"F8.opExtrude","SWEPT_FACE",FACE,{"disambiguationData":[OSD([sQuery(id+"F7.wireOp",EDGE,"E36.1")])]})}),makeQuery(id+"F8.boolean.opBoolean","COPY",FACE,{"derivedFrom":makeQuery(id+"F8.opExtrude","SWEPT_FACE",FACE,{"disambiguationData":[OSD([sQuery(id+"F7.wireOp",EDGE,"E45.0.3.1"),sQuery(id+"F7.wireOp",EDGE,"E45.0.3.3"),sQuery(id+"F7.wireOp",EDGE,"E45.0.3.5")])]})}),makeQuery(id+"F8.boolean.opBoolean","COPY",FACE,{"derivedFrom":makeQuery(id+"F8.opExtrude","SWEPT_FACE",FACE,{"disambiguationData":[OSD([sQuery(id+"F7.wireOp",EDGE,"E45.0.3.2"),sQuery(id+"F7.wireOp",EDGE,"E45.0.3.4"),sQuery(id+"F7.wireOp",EDGE,"E45.0.3.6")])]})}),makeQuery(id+"F8.boolean.opBoolean","COPY",FACE,{"derivedFrom":makeQuery(id+"F8.opExtrude","SWEPT_FACE",FACE,{"disambiguationData":[OSD([sQuery(id+"F7.wireOp",EDGE,"E45.0.3.7")])]})}),makeQuery(id+"F10.opExtrude","SWEPT_FACE",FACE,{"disambiguationData":[OSD([sQuery(id+"F9.wireOp",EDGE,"E46.0")])]}),makeQuery(id+"F10.opExtrude","SWEPT_FACE",FACE,{"disambiguationData":[OSD([sQuery(id+"F9.wireOp",EDGE,"E46.1")])]}),makeQuery(id+"F10.opExtrude","SWEPT_FACE",FACE,{"disambiguationData":[OSD([sQuery(id+"F9.wireOp",EDGE,"E48.0.left"),sQuery(id+"F9.wireOp",EDGE,"E49"),sQuery(id+"F9.wireOp",EDGE,"E52")])]}),makeQuery(id+"F10.opExtrude","SWEPT_FACE",FACE,{"disambiguationData":[OSD([sQuery(id+"F9.wireOp",EDGE,"E48.0.right"),sQuery(id+"F9.wireOp",EDGE,"E50"),sQuery(id+"F9.wireOp",EDGE,"E51")])]}),makeQuery(id+"F10.opExtrude","SWEPT_FACE",FACE,{"disambiguationData":[OSD([sQuery(id+"F9.wireOp",EDGE,"E53.1.0.0")])]}),makeQuery(id+"F10.opExtrude","SWEPT_FACE",FACE,{"disambiguationData":[OSD([sQuery(id+"F9.wireOp",EDGE,"E53.1.0.1"),sQuery(id+"F9.wireOp",EDGE,"E53.1.0.4"),sQuery(id+"F9.wireOp",EDGE,"E53.1.0.5")])]}),makeQuery(id+"F10.opExtrude","SWEPT_FACE",FACE,{"disambiguationData":[OSD([sQuery(id+"F9.wireOp",EDGE,"E53.1.0.2"),sQuery(id+"F9.wireOp",EDGE,"E53.1.0.3"),sQuery(id+"F9.wireOp",EDGE,"E53.1.0.6")])]}),makeQuery(id+"F10.opExtrude","SWEPT_FACE",FACE,{"disambiguationData":[OSD([sQuery(id+"F9.wireOp",EDGE,"E53.1.0.7")])]}),makeQuery(id+"F10.opExtrude","SWEPT_FACE",FACE,{"disambiguationData":[OSD([sQuery(id+"F9.wireOp",EDGE,"E53.2.0.0")])]}),makeQuery(id+"F10.opExtrude","SWEPT_FACE",FACE,{"disambiguationData":[OSD([sQuery(id+"F9.wireOp",EDGE,"E53.2.0.1"),sQuery(id+"F9.wireOp",EDGE,"E53.2.0.4"),sQuery(id+"F9.wireOp",EDGE,"E53.2.0.5")])]}),makeQuery(id+"F10.opExtrude","SWEPT_FACE",FACE,{"disambiguationData":[OSD([sQuery(id+"F9.wireOp",EDGE,"E53.2.0.2"),sQuery(id+"F9.wireOp",EDGE,"E53.2.0.3"),sQuery(id+"F9.wireOp",EDGE,"E53.2.0.6")])]}),makeQuery(id+"F10.opExtrude","SWEPT_FACE",FACE,{"disambiguationData":[OSD([sQuery(id+"F9.wireOp",EDGE,"E53.2.0.7")])]}),makeQuery(id+"F10.opExtrude","SWEPT_FACE",FACE,{"disambiguationData":[OSD([sQuery(id+"F9.wireOp",EDGE,"E53.3.0.0")])]}),makeQuery(id+"F10.opExtrude","SWEPT_FACE",FACE,{"disambiguationData":[OSD([sQuery(id+"F9.wireOp",EDGE,"E53.3.0.1"),sQuery(id+"F9.wireOp",EDGE,"E53.3.0.4"),sQuery(id+"F9.wireOp",EDGE,"E53.3.0.5")])]}),makeQuery(id+"F10.opExtrude","SWEPT_FACE",FACE,{"disambiguationData":[OSD([sQuery(id+"F9.wireOp",EDGE,"E53.3.0.2"),sQuery(id+"F9.wireOp",EDGE,"E53.3.0.3"),sQuery(id+"F9.wireOp",EDGE,"E53.3.0.6")])]}),makeQuery(id+"F10.opExtrude","SWEPT_FACE",FACE,{"disambiguationData":[OSD([sQuery(id+"F9.wireOp",EDGE,"E53.3.0.7")])]}),makeQuery(id+"F10.opExtrude","SWEPT_FACE",FACE,{"disambiguationData":[OSD([sQuery(id+"F9.wireOp",EDGE,"E53.4.0.0")])]}),makeQuery(id+"F10.opExtrude","SWEPT_FACE",FACE,{"disambiguationData":[OSD([sQuery(id+"F9.wireOp",EDGE,"E53.4.0.1"),sQuery(id+"F9.wireOp",EDGE,"E53.4.0.4"),sQuery(id+"F9.wireOp",EDGE,"E53.4.0.5")])]}),makeQuery(id+"F10.opExtrude","SWEPT_FACE",FACE,{"disambiguationData":[OSD([sQuery(id+"F9.wireOp",EDGE,"E53.4.0.2"),sQuery(id+"F9.wireOp",EDGE,"E53.4.0.3"),sQuery(id+"F9.wireOp",EDGE,"E53.4.0.6")])]}),makeQuery(id+"F10.opExtrude","SWEPT_FACE",FACE,{"disambiguationData":[OSD([sQuery(id+"F9.wireOp",EDGE,"E53.4.0.7")])]}),makeQuery(id+"F10.opExtrude","SWEPT_FACE",FACE,{"disambiguationData":[OSD([sQuery(id+"F9.wireOp",EDGE,"E53.5.0.0")])]}),makeQuery(id+"F10.opExtrude","SWEPT_FACE",FACE,{"disambiguationData":[OSD([sQuery(id+"F9.wireOp",EDGE,"E53.5.0.1"),sQuery(id+"F9.wireOp",EDGE,"E53.5.0.4"),sQuery(id+"F9.wireOp",EDGE,"E53.5.0.5")])]}),makeQuery(id+"F10.opExtrude","SWEPT_FACE",FACE,{"disambiguationData":[OSD([sQuery(id+"F9.wireOp",EDGE,"E53.5.0.2"),sQuery(id+"F9.wireOp",EDGE,"E53.5.0.3"),sQuery(id+"F9.wireOp",EDGE,"E53.5.0.6")])]}),makeQuery(id+"F10.opExtrude","SWEPT_FACE",FACE,{"disambiguationData":[OSD([sQuery(id+"F9.wireOp",EDGE,"E53.5.0.7")])]}),makeQuery(id+"F10.opExtrude","SWEPT_FACE",FACE,{"disambiguationData":[OSD([sQuery(id+"F9.wireOp",EDGE,"E53.6.0.0")])]}),makeQuery(id+"F10.opExtrude","SWEPT_FACE",FACE,{"disambiguationData":[OSD([sQuery(id+"F9.wireOp",EDGE,"E53.6.0.1"),sQuery(id+"F9.wireOp",EDGE,"E53.6.0.4"),sQuery(id+"F9.wireOp",EDGE,"E53.6.0.5")])]}),makeQuery(id+"F10.opExtrude","SWEPT_FACE",FACE,{"disambiguationData":[OSD([sQuery(id+"F9.wireOp",EDGE,"E53.6.0.2"),sQuery(id+"F9.wireOp",EDGE,"E53.6.0.3"),sQuery(id+"F9.wireOp",EDGE,"E53.6.0.6")])]}),makeQuery(id+"F10.opExtrude","SWEPT_FACE",FACE,{"disambiguationData":[OSD([sQuery(id+"F9.wireOp",EDGE,"E53.6.0.7")])]}),makeQuery(id+"F10.opExtrude","SWEPT_FACE",FACE,{"disambiguationData":[OSD([sQuery(id+"F9.wireOp",EDGE,"E53.7.0.0")])]}),makeQuery(id+"F10.opExtrude","SWEPT_FACE",FACE,{"disambiguationData":[OSD([sQuery(id+"F9.wireOp",EDGE,"E53.7.0.1"),sQuery(id+"F9.wireOp",EDGE,"E53.7.0.4"),sQuery(id+"F9.wireOp",EDGE,"E53.7.0.5")])]}),makeQuery(id+"F10.opExtrude","SWEPT_FACE",FACE,{"disambiguationData":[OSD([sQuery(id+"F9.wireOp",EDGE,"E53.7.0.2"),sQuery(id+"F9.wireOp",EDGE,"E53.7.0.3"),sQuery(id+"F9.wireOp",EDGE,"E53.7.0.6")])]}),makeQuery(id+"F10.opExtrude","SWEPT_FACE",FACE,{"disambiguationData":[OSD([sQuery(id+"F9.wireOp",EDGE,"E53.7.0.7")])]})])],"derivedFrom":makeQuery(id+"F4.opExtrude","CAP_FACE",FACE,{"disambiguationData":[OSD([subQ0,subQ2,subQ3,subQ1,subQ4,subQ5,subQ6,subQ7,subQ8,subQ9,subQ10,subQ11])],"isStart":false})});}
            extrude(context, id + "F12", {"entities" : qUnion([Q0]), "operationType" : NewBodyOperationType.REMOVE, "endBound" : BoundingType.UP_TO_SURFACE, "endBoundEntityFace" : qUnion([Q1]), "depth" : 25 * mm});
        }
    });
